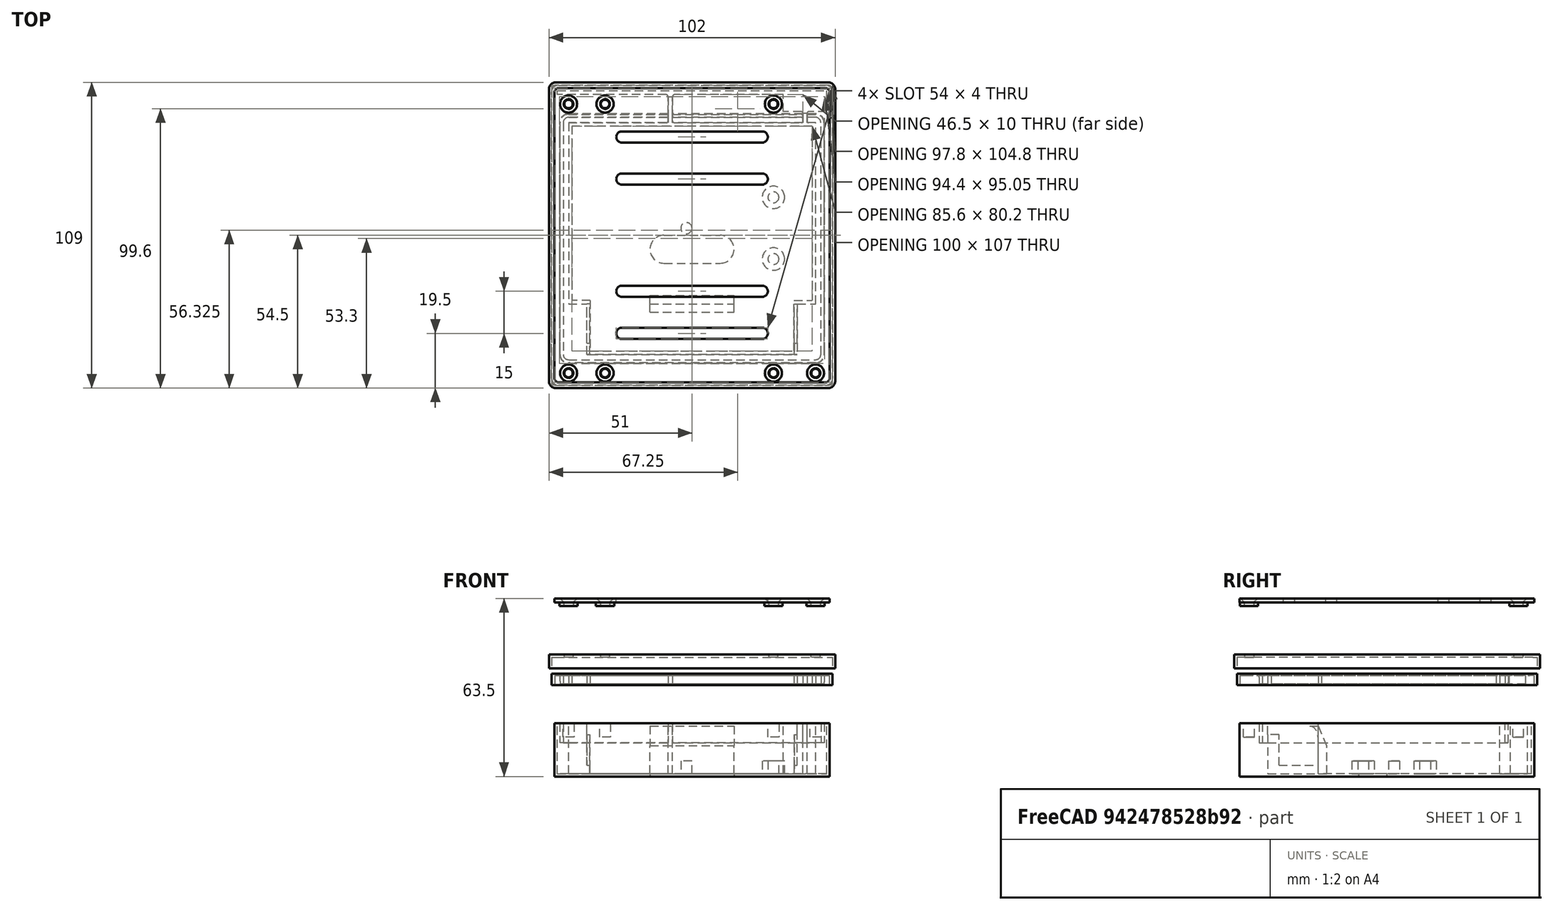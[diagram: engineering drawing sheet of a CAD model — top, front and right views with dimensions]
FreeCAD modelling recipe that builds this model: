
FCSTD DOCUMENT  (FreeCAD 1.0R39319 (Git))
Label: RAKTracker-v11
License: All rights reserved
objects: Sketcher::SketchObject×19, PartDesign::Pad×13, PartDesign::Pocket×4, PartDesign::Body×4, PartDesign::SubShapeBinder×3, PartDesign::Plane×2, Spreadsheet::Sheet×1, PartDesign::AdditiveLoft×1, PartDesign::Hole×1
note: 104 computed .brp shape members not serialized (recipe doc carries the construction recipe); baked Part::Feature solids carry a one-line shape summary decoded from their .brp

FEATURE [Spreadsheet::Sheet] Spreadsheet  label="sheet"
  cells = A1='Components; D1='None-Component sizes; D3='M3 Insert Hole Dia; E3(InsetDiaM3)==3.9 mm; A4='Solar Panel; D4='M2.5 Insert Hole DIa; E4(InsertDiaM2_5)==3.9 mm; A5='Panel width; B5(PanelWidth)==95 mm; D5='M3 Though Hall; E5(M3ThoughHoleDia)==3.2 mm; A6='Panel length; B6(PanelLength)==95 mm; D6='Insert Hole Depth; E6(InsertDepth)==8 mm; A7='Panel height; B7==1.5 mm; D8='PCB Mount Outer Diameter; E8(PCBMountDia)==8 mm; A9='Battery; D9='PCB Mount Height; E9(PCBMountHeight)==4.5 mm; A10='Battery Width; B10(BatteryWidth)==18 mm; D10='PCB Mount from Side; E10(PCBMountFromSide)==15 mm; A11='Battery Length; B11(BatteryLength)==65 mm; A12='Battery Height; B12(BatteryHeight)==18 mm; A13='Battery Mount Distance; B13(BatteryMountDistance)==75 mm; D14='Lid Wall Around sides; E14(LidWallAroundSides)==1 mm; A15='GPS Antenna Width; B15==15.5 mm; D15='Lid Wall Margin; E15==0.25 mm; A16='GPS Antenna Height; B16(AntGPSHeight)==7.5 mm; D16='Strap Mount Dia; E16(StrapMountDia)==8 mm; A17='GPS Antenna Length; B17(AntGPSLength)==15.5 mm; D17='Strap slot width; E17(StrapSlotWidth)==2 mm; D18='Strap slot distance; E18(StrapSlotDistance)==60 mm; A19='Small Molex Lora Antenna Width; B19(AntSmallLoraWidth)==10 mm; A20='Small Molex Lora Antenna Length; B20(AntSmallLoraLength)==80 mm; D20='SealWidth; E20(SealWidthTop)==1.2 mm; A21='Small Molex Lora Antenna Height; B21(AntSmallLoraHeight)==1.4 mm; D21='SealHeight; E21(SealHeight)==3 mm; D22='SealOuterWidth; E22(SealOuterWidth)==1 mm; A23='Large Molex Lora Antenna Width Sticker; B23(AntLargeLoraWidth)==12.5 mm; D23='Wall Width; E23(WallWidth)==5 mm; A24='Large Molex Lora Antenna Length Sticker; B24(AntLargeLoraLength)==87.5 mm; A25='Large Molex Lora Antenna Width (white); B25='TBD; A26='Large Molex Lora Antenna Length (white); B26==100 mm; D26='Bottom Thickness; E26(WallBottomThickness)==1 mm; A27='Large Molex Lora Antenna Height; B27(AntLargeLoraHeight)==1.6 mm; D27='Box Corner Radisu; E27(BoxCornerRadius)==1.5 mm; D28='BoxAntennaSpace; E28(BoxAntennaSpace)==10 mm; A29='Antenna Wire width; B29(AntWireWidth)==1.5 mm; A31='PCB Width; B31==30 mm; A32='PCB Length; B32==38 mm; A33='PCB Width With Margin; B33==31 mm; A34='PCB Length with Margin; B34==39 mm; A35='PCB Height; B35==16 mm; A36='PCB 2 Hole Distance; B36(PCBHoleDistance)==22 mm; A37='PCB Single Hole Distance from 2 Holes; B37(PCBHoleAwayFrom2Holes)==31 mm
FEATURE [Sketcher::SketchObject] Sketch  label="BoxBaseSketch"
  ArcFitTolerance = 1e-06
  AttachmentSupport = -> [XY_Plane]
  FullyConstrained = true
  MakeInternals = false
  MapMode = 5
  expr: Constraints[18] = <<sheet>>.BoxCornerRadius
  expr: Constraints[28] = <<sheet>>.PanelLength
  expr: Constraints[29] = <<sheet>>.PanelWidth
  expr: Constraints[31] = <<sheet>>.BoxAntennaSpace
  expr: Constraints[40] = <<sheet>>.PanelWidth / 2
  sketch-geometry (18):
    g0: LineSegment StartX=-47.5 StartY=-52.5 StartZ=0 EndX=47.5 EndY=-52.5 EndZ=0
    g1: LineSegment StartX=49 StartY=-51 StartZ=0 EndX=49 EndY=51 EndZ=0
    g2: LineSegment StartX=47.5 StartY=52.5 StartZ=0 EndX=-47.5 EndY=52.5 EndZ=0
    g3: LineSegment StartX=-49 StartY=51 StartZ=0 EndX=-49 EndY=-51 EndZ=0
    g4: ArcOfCircle CenterX=-47.5 CenterY=-51 CenterZ=0 NormalX=0 NormalY=0 NormalZ=1 AngleXU=0 Radius=1.5 StartAngle=3.14159 EndAngle=4.71239
    g5: ArcOfCircle CenterX=47.5 CenterY=-51 CenterZ=0 NormalX=0 NormalY=0 NormalZ=1 AngleXU=0 Radius=1.5 StartAngle=4.71239 EndAngle=6.28319
    g6: ArcOfCircle CenterX=47.5 CenterY=51 CenterZ=0 NormalX=0 NormalY=0 NormalZ=1 AngleXU=0 Radius=1.5 StartAngle=8e-16 EndAngle=1.5708
    g7: ArcOfCircle CenterX=-47.5 CenterY=51 CenterZ=0 NormalX=0 NormalY=0 NormalZ=1 AngleXU=0 Radius=1.5 StartAngle=1.5708 EndAngle=3.14159
    g8: GeomPoint [constr] X=49 Y=52.5 Z=0
    g9: GeomPoint [constr] X=0 Y=0 Z=0
    g10: LineSegment [constr] StartX=47.5 StartY=-52.5 StartZ=0 EndX=47.5 EndY=42.5 EndZ=0
    g11: LineSegment [constr] StartX=47.5 StartY=42.5 StartZ=0 EndX=-47.5 EndY=42.5 EndZ=0
    g12: LineSegment [constr] StartX=-47.5 StartY=42.5 StartZ=0 EndX=-47.5 EndY=-52.5 EndZ=0
    g13: LineSegment [constr] StartX=-47.5 StartY=-52.5 StartZ=0 EndX=47.5 EndY=-52.5 EndZ=0
    g14: ArcOfCircle CenterX=-10 CenterY=-5 CenterZ=0 NormalX=0 NormalY=0 NormalZ=1 AngleXU=0 Radius=5 StartAngle=1.5708 EndAngle=4.71239
    g15: ArcOfCircle CenterX=10 CenterY=-5 CenterZ=0 NormalX=0 NormalY=0 NormalZ=1 AngleXU=0 Radius=5 StartAngle=4.71239 EndAngle=7.85398
    g16: LineSegment StartX=-10 StartY=0 StartZ=0 EndX=10 EndY=0 EndZ=0
    g17: LineSegment StartX=-10 StartY=-10 StartZ=0 EndX=10 EndY=-10 EndZ=0
  constraints (41):
    c: Tangent(g0,g4) = -1.5708
    c: Tangent(g0,g5) = -1.5708
    c: Tangent(g1,g5) = -1.5708
    c: Tangent(g1,g6) = -1.5708
    c: Tangent(g2,g6) = -1.5708
    c: Tangent(g2,g7) = -1.5708
    c: Tangent(g3,g7) = -1.5708
    c: Tangent(g3,g4) = -1.5708
    c: Horizontal(g0)
    c: Horizontal(g2)
    c: Vertical(g1)
    c: Vertical(g3)
    c: Equal(g4,g5)
    c: Equal(g5,g6)
    c: Equal(g6,g7)
    c: Symmetric(g2,g0,g9)
    c: PointOnObject(g8,g1)
    c: PointOnObject(g8,g2)
    c: Radius(g5) = 1.5
    c: Coincident(g9,g-1)
    c: Coincident(g10,g11)
    c: Coincident(g11,g12)
    c: Coincident(g12,g13)
    c: Coincident(g13,g10)
    c: Vertical(g10)
    c: Vertical(g12)
    c: Horizontal(g11)
    c: Coincident(g10,g0)
    c: DistanceX(g12,g0) = 95
    c: DistanceY(g10,g10) = 95
    c: Coincident(g12,g0)
    c: DistanceY(g10,g2) = 10
    c: Tangent(g14,g16) = 1.5708
    c: Tangent(g14,g17) = -1.5708
    c: Tangent(g15,g16) = 1.5708
    c: Tangent(g15,g17) = -1.5708
    c: Equal(g14,g15)
    c: Distance(g15,g15) = 10
    c: DistanceX(g14,g15) = 20
    c: Symmetric(g14,g15,g-2)
    c: DistanceY(g15,g10) = 47.5
FEATURE [PartDesign::Pad] Pad  label="BoxBase"
  Direction = (0,0,1)
  Length = 1
  Length2 = 10
  Profile = -> Sketch
  ReferenceAxis = -> Sketch [N_Axis]
  Suppressed = false
  Type = 0
  expr: Length = <<sheet>>.WallBottomThickness
FEATURE [Sketcher::SketchObject] Sketch001  label="BoxOuterWallSketch"
  ArcFitTolerance = 1e-06
  AttachmentSupport = -> [XY_Plane]
  FullyConstrained = true
  MakeInternals = false
  MapMode = 5
  expr: Constraints[100] = <<sheet>>.PanelWidth
  expr: Constraints[101] = <<sheet>>.PanelLength
  expr: Constraints[103] = <<sheet>>.BoxAntennaSpace
  expr: Constraints[115] = <<sheet>>.BoxCornerRadius
  expr: Constraints[129] = <<sheet>>.WallWidth
  expr: Constraints[49] = <<sheet>>.AntGPSLength
  expr: Constraints[50] = <<sheet>>.AntWireWidth
  expr: Constraints[51] = <<sheet>>.BatteryMountDistance
  expr: Constraints[52] = <<sheet>>.WallWidth * 2
  expr: Constraints[53] = <<sheet>>.WallWidth
  expr: Constraints[54] = <<sheet>>.BatteryWidth
  expr: Constraints[87] = <<sheet>>.AntWireWidth
  expr: Constraints[90] = <<sheet>>.AntSmallLoraHeight
  expr: Constraints[91] = <<sheet>>.AntGPSHeight
  expr: Constraints[92] = <<sheet>>.WallWidth * 2
  sketch-geometry (48):
    g0: LineSegment StartX=-47.5 StartY=-52.5 StartZ=0 EndX=47.5 EndY=-52.5 EndZ=0
    g1: LineSegment StartX=49 StartY=-51 StartZ=0 EndX=49 EndY=51 EndZ=0
    g2: LineSegment StartX=47.5 StartY=52.5 StartZ=0 EndX=-47.5 EndY=52.5 EndZ=0
    g3: LineSegment StartX=44 StartY=40.1 StartZ=0 EndX=44 EndY=-24.5 EndZ=0
    g4: LineSegment StartX=44 StartY=-24.5 StartZ=0 EndX=37.5 EndY=-24.5 EndZ=0
    g5: LineSegment StartX=37.5 StartY=-24.5 StartZ=0 EndX=37.5 EndY=-42.5 EndZ=0
    g6: LineSegment StartX=37.5 StartY=-42.5 StartZ=0 EndX=-37.5 EndY=-42.5 EndZ=0
    g7: LineSegment StartX=-37.5 StartY=-42.5 StartZ=0 EndX=-37.5 EndY=-24.5 EndZ=0
    g8: LineSegment StartX=-37.5 StartY=-24.5 StartZ=0 EndX=-44 EndY=-24.5 EndZ=0
    g9: LineSegment StartX=-44 StartY=-24.5 StartZ=0 EndX=-44 EndY=40.1 EndZ=0
    g10: LineSegment StartX=-44 StartY=40.1 StartZ=0 EndX=-9.25 EndY=40.1 EndZ=0
    g11: LineSegment StartX=-8.5 StartY=40.85 StartZ=0 EndX=-8.5 EndY=49.35 EndZ=0
    g12: LineSegment StartX=-9.25 StartY=50.1 StartZ=0 EndX=-48 EndY=50.1 EndZ=0
    g13: LineSegment StartX=-48 StartY=50.1 StartZ=0 EndX=-48 EndY=51.5 EndZ=0
    g14: LineSegment StartX=-48 StartY=51.5 StartZ=0 EndX=48 EndY=51.5 EndZ=0
    g15: LineSegment StartX=-7 StartY=40.85 StartZ=0 EndX=-7 EndY=49.35 EndZ=0
    g16: LineSegment StartX=-6.25 StartY=50.1 StartZ=0 EndX=32.5 EndY=50.1 EndZ=0
    g17: LineSegment StartX=32.5 StartY=50.1 StartZ=0 EndX=32.5 EndY=44 EndZ=0
    g18: LineSegment StartX=48 StartY=44 StartZ=0 EndX=48 EndY=51.5 EndZ=0
    g19: ArcOfCircle CenterX=-9.25 CenterY=49.35 CenterZ=0 NormalX=0 NormalY=0 NormalZ=1 AngleXU=0 Radius=0.75 StartAngle=2e-15 EndAngle=1.5708
    g20: GeomPoint [constr] X=-8.5 Y=50.1 Z=0
    g21: ArcOfCircle CenterX=-6.25 CenterY=49.35 CenterZ=0 NormalX=0 NormalY=0 NormalZ=1 AngleXU=0 Radius=0.75 StartAngle=1.5708 EndAngle=3.14159
    g22: ArcOfCircle CenterX=-9.25 CenterY=40.85 CenterZ=0 NormalX=0 NormalY=0 NormalZ=1 AngleXU=0 Radius=0.75 StartAngle=4.71239 EndAngle=6.28319
    g23: GeomPoint [constr] X=-8.5 Y=40.1 Z=0
    g24: ArcOfCircle CenterX=-6.25 CenterY=40.85 CenterZ=0 NormalX=0 NormalY=0 NormalZ=1 AngleXU=0 Radius=0.75 StartAngle=3.14159 EndAngle=4.71239
    g25: LineSegment StartX=32.5 StartY=44 StartZ=0 EndX=39 EndY=44 EndZ=0
    g26: LineSegment StartX=39.5 StartY=43.5 StartZ=0 EndX=39.5 EndY=40.6 EndZ=0
    g27: LineSegment StartX=39 StartY=40.1 StartZ=0 EndX=-6.25 EndY=40.1 EndZ=0
    g28: LineSegment StartX=48 StartY=44 StartZ=0 EndX=41.5 EndY=44 EndZ=0
    g29: LineSegment StartX=41 StartY=43.5 StartZ=0 EndX=41 EndY=40.6 EndZ=0
    g30: LineSegment StartX=41.5 StartY=40.1 StartZ=0 EndX=44 EndY=40.1 EndZ=0
    g31: ArcOfCircle CenterX=39 CenterY=43.5 CenterZ=0 NormalX=0 NormalY=0 NormalZ=1 AngleXU=0 Radius=0.5 StartAngle=-1.8e-15 EndAngle=1.5708
    g32: GeomPoint [constr] X=39.5 Y=44 Z=0
    g33: ArcOfCircle CenterX=41.5 CenterY=43.5 CenterZ=0 NormalX=0 NormalY=0 NormalZ=1 AngleXU=0 Radius=0.5 StartAngle=1.5708 EndAngle=3.14159
    g34: GeomPoint [constr] X=41 Y=44 Z=0
    g35: ArcOfCircle CenterX=39 CenterY=40.6 CenterZ=0 NormalX=0 NormalY=0 NormalZ=1 AngleXU=0 Radius=0.5 StartAngle=4.71239 EndAngle=6.28319
    g36: GeomPoint [constr] X=39.5 Y=40.1 Z=0
    g37: ArcOfCircle CenterX=41.5 CenterY=40.6 CenterZ=0 NormalX=0 NormalY=0 NormalZ=1 AngleXU=0 Radius=0.5 StartAngle=3.14159 EndAngle=4.71239
    g38: GeomPoint [constr] X=41 Y=40.1 Z=0
    g39: LineSegment [constr] StartX=-47.5 StartY=42.5 StartZ=0 EndX=-47.5 EndY=-52.5 EndZ=0
    g40: LineSegment [constr] StartX=-47.5 StartY=-52.5 StartZ=0 EndX=47.5 EndY=-52.5 EndZ=0
    g41: LineSegment [constr] StartX=47.5 StartY=-52.5 StartZ=0 EndX=47.5 EndY=42.5 EndZ=0
    g42: LineSegment [constr] StartX=47.5 StartY=42.5 StartZ=0 EndX=-47.5 EndY=42.5 EndZ=0
    g43: LineSegment StartX=-49 StartY=51 StartZ=0 EndX=-49 EndY=-51 EndZ=0
    g44: ArcOfCircle CenterX=-47.5 CenterY=-51 CenterZ=0 NormalX=0 NormalY=0 NormalZ=1 AngleXU=0 Radius=1.5 StartAngle=3.14159 EndAngle=4.71239
    g45: ArcOfCircle CenterX=47.5 CenterY=-51 CenterZ=0 NormalX=0 NormalY=0 NormalZ=1 AngleXU=0 Radius=1.5 StartAngle=4.71239 EndAngle=6.28319
    g46: ArcOfCircle CenterX=47.5 CenterY=51 CenterZ=0 NormalX=0 NormalY=0 NormalZ=1 AngleXU=0 Radius=1.5 StartAngle=0 EndAngle=1.5708
    g47: ArcOfCircle CenterX=-47.5 CenterY=51 CenterZ=0 NormalX=0 NormalY=0 NormalZ=1 AngleXU=0 Radius=1.5 StartAngle=1.5708 EndAngle=3.14159
  constraints (132):
    c: Vertical(g1)
    c: Horizontal(g2)
    c: Vertical(g3)
    c: Coincident(g3,g4)
    c: Horizontal(g4)
    c: Coincident(g4,g5)
    c: Vertical(g5)
    c: Coincident(g5,g6)
    c: Horizontal(g6)
    c: Coincident(g6,g7)
    c: Vertical(g7)
    c: Coincident(g7,g8)
    c: Coincident(g8,g9)
    c: Vertical(g9)
    c: Coincident(g9,g10)
    c: Horizontal(g10)
    c: Coincident(g12,g13)
    c: Coincident(g13,g14)
    c: Horizontal(g14)
    c: Horizontal(g8)
    c: Vertical(g15)
    c: Horizontal(g16)
    c: Coincident(g16,g17)
    c: Coincident(g18,g14)
    c: Vertical(g18)
    c: Vertical(g17)
    c: Vertical(g11)
    c: Vertical(g13)
    c: Horizontal(g12)
    c: PointOnObject(g20,g12)
    c: PointOnObject(g20,g11)
    c: Tangent(g12,g19) = -1.5708
    c: Tangent(g11,g19) = -1.5708
    c: Tangent(g15,g21) = 1.5708
    c: Tangent(g16,g21) = 1.5708
    c: PointOnObject(g23,g11)
    c: PointOnObject(g23,g10)
    c: Tangent(g11,g22) = -1.5708
    c: Tangent(g10,g22) = -1.5708
    c: Tangent(g15,g24) = 1.5708
    c: Radius(g19) = 0.75
    c: Equal(g19,g22)
    c: Equal(g22,g21)
    c: Equal(g21,g24)
    c: Horizontal(g11,g15)
    c: Horizontal(g7,g4)
    c: Equal(g8,g4)
    c: DistanceY(g13,g2) = 1
    c: DistanceX(g14,g1) = 1
    c: DistanceX(g17,g18) = 15.5
    c: DistanceX(g11,g15) = 1.5
    c: DistanceX(g7,g4) = 75
    c: DistanceY(g0,g6) = 10
    c: DistanceX(g3,g1) = 5
    c: DistanceY(g5,g4) = 18
    c: Coincident(g17,g25)
    c: Coincident(g27,g24)
    c: Horizontal(g27)
    c: Coincident(g18,g28)
    c: Horizontal(g28)
    c: Coincident(g30,g3)
    c: Horizontal(g25)
    c: Vertical(g29)
    c: Vertical(g26)
    c: Horizontal(g30)
    c: PointOnObject(g32,g25)
    c: PointOnObject(g32,g26)
    c: Tangent(g25,g31) = 1.5708
    c: Tangent(g26,g31) = 1.5708
    c: PointOnObject(g34,g29)
    c: PointOnObject(g34,g28)
    c: Tangent(g29,g33) = -1.5708
    c: Tangent(g28,g33) = -1.5708
    c: PointOnObject(g36,g26)
    c: PointOnObject(g36,g27)
    c: Tangent(g26,g35) = 1.5708
    c: Tangent(g27,g35) = 1.5708
    c: PointOnObject(g38,g30)
    c: PointOnObject(g38,g29)
    c: Tangent(g30,g37) = -1.5708
    c: Tangent(g29,g37) = -1.5708
    c: Radius(g31) = 0.5
    c: Equal(g31,g33)
    c: Equal(g33,g35)
    c: Equal(g35,g37)
    c: Horizontal(g30,g27)
    c: Horizontal(g25,g28)
    c: DistanceX(g26,g29) = 1.5
    c: Equal(g25,g28)
    c: Horizontal(g10,g24)
    c: DistanceY(g12,g13) = 1.4
    c: DistanceY(g18,g14) = 7.5
    c: DistanceY(g9,g12) = 10
    c: Coincident(g39,g40)
    c: Coincident(g41,g42)
    c: Coincident(g42,g39)
    c: Vertical(g39)
    c: Vertical(g41)
    c: Horizontal(g42)
    c: Horizontal(g0)
    c: DistanceY(g39,g39) = 95
    c: DistanceX(g40,g40) = 95
    c: Coincident(g41,g40)
    c: DistanceY(g41,g2) = 10
    c: Coincident(g0,g39)
    c: Coincident(g0,g40)
    c: Vertical(g43)
    c: Coincident(g44,g0)
    c: Coincident(g44,g43)
    c: Coincident(g45,g0)
    c: Coincident(g45,g1)
    c: Coincident(g46,g2)
    c: Coincident(g46,g1)
    c: Coincident(g47,g43)
    c: Coincident(g47,g2)
    c: Radius(g47) = 1.5
    c: Horizontal(g47,g43)
    c: Vertical(g47,g2)
    c: Equal(g47,g46)
    c: Vertical(g2,g46)
    c: Horizontal(g1,g46)
    c: Vertical(g44,g0)
    c: Horizontal(g43,g44)
    c: Horizontal(g1,g45)
    c: Vertical(g0,g45)
    c: DistanceX(g43,g12) = 1
    c: Symmetric(g2,g0,g-1)
    c: Vertical(g39,g47)
    c: Vertical(g41,g46)
    c: DistanceX(g43,g8) = 5
    c: DistanceX(g12,g11) = 39.5
    c: Horizontal(g12,g16)
FEATURE [PartDesign::Pad] Pad001  label="BoxWall"
  BaseFeature = -> Pad
  Direction = (0,0,1)
  Length = 19
  Length2 = 10
  Profile = -> Sketch001
  ReferenceAxis = -> Sketch001 [N_Axis]
  Suppressed = false
  Type = 0
  expr: Length = <<sheet>>.BatteryWidth + <<sheet>>.WallBottomThickness
FEATURE [Sketcher::SketchObject] Sketch002  label="BoxPCBMountSketch"
  ArcFitTolerance = 1e-06
  AttachmentSupport = -> [XY_Plane]
  ExternalGeometry = -> [Sketch001]
  FullyConstrained = true
  MakeInternals = false
  MapMode = 5
  expr: Constraints[10] = <<sheet>>.PCBHoleDistance / 2
  expr: Constraints[11] = <<sheet>>.PCBMountFromSide
  expr: Constraints[2] = <<sheet>>.InsetDiaM3
  expr: Constraints[5] = <<sheet>>.PCBMountDia
  expr: Constraints[7] = <<sheet>>.PCBHoleDistance
  expr: Constraints[8] = <<sheet>>.PCBHoleAwayFrom2Holes
  expr: Constraints[9] = <<sheet>>.PCBMountDia / 2
  sketch-geometry (5):
    g0: Circle CenterX=29 CenterY=13.5 CenterZ=0 NormalX=0 NormalY=0 NormalZ=1 AngleXU=0 Radius=4
    g1: Circle CenterX=29 CenterY=-8.5 CenterZ=0 NormalX=0 NormalY=0 NormalZ=1 AngleXU=0 Radius=4
    g2: Circle CenterX=29 CenterY=-8.5 CenterZ=0 NormalX=0 NormalY=0 NormalZ=1 AngleXU=0 Radius=1.95
    g3: Circle CenterX=29 CenterY=13.5 CenterZ=0 NormalX=0 NormalY=0 NormalZ=1 AngleXU=0 Radius=1.95
    g4: Circle CenterX=-2 CenterY=2.5 CenterZ=0 NormalX=0 NormalY=0 NormalZ=1 AngleXU=0 Radius=2
  constraints (13):
    c: Coincident(g2,g1)
    c: Coincident(g3,g0)
    c: Diameter(g3) = 3.9
    c: Equal(g3,g2)
    c: Vertical(g1,g0)
    c: Diameter(g0) = 8
    c: Equal(g0,g1)
    c: DistanceY(g1,g0) = 22
    c: DistanceX(g4,g1) = 31
    c: Diameter(g4) = 4
    c: DistanceY(g1,g4) = 11
    c: DistanceX(g1,g-3) = 15
    c: DistanceY(g-3,g1) = 16
FEATURE [PartDesign::Pad] Pad002  label="BoxPCBMount"
  BaseFeature = -> Pad001
  Direction = (0,0,1)
  Length = 5.5
  Length2 = 10
  Profile = -> Sketch002
  ReferenceAxis = -> Sketch002 [N_Axis]
  Suppressed = false
  Type = 0
  expr: Length = <<sheet>>.WallBottomThickness + <<sheet>>.PCBMountHeight
FEATURE [Sketcher::SketchObject] Sketch003  label="BoxBatteryHolderSketch"
  ArcFitTolerance = 1e-06
  AttachmentSupport = -> [YZ_Plane]
  ExternalGeometry = -> [Sketch001]
  FullyConstrained = true
  MakeInternals = false
  MapMode = 5
  Placement = pos=(0,0,0) rot=(0.57735,0.57735,0.57735;2.0944rad)
  expr: Constraints[21] = <<sheet>>.BatteryWidth
  sketch-geometry (11):
    g0: LineSegment StartX=-24.5 StartY=0 StartZ=0 EndX=-24.5 EndY=11 EndZ=0
    g1: LineSegment StartX=-24.5 StartY=0 StartZ=0 EndX=-21.5 EndY=0 EndZ=0
    g2: LineSegment StartX=-21.5 StartY=0 StartZ=0 EndX=-21.5 EndY=11 EndZ=0
    g3: Circle [constr] CenterX=-27.5 CenterY=18 CenterZ=0 NormalX=0 NormalY=0 NormalZ=1 AngleXU=0 Radius=1
    g4: Circle [constr] CenterX=-24.5 CenterY=18 CenterZ=0 NormalX=0 NormalY=0 NormalZ=1 AngleXU=0 Radius=1
    g5: Circle [constr] CenterX=-24.5 CenterY=11 CenterZ=0 NormalX=0 NormalY=0 NormalZ=1 AngleXU=0 Radius=1
    g6: BSplineCurve PolesCount=3 KnotsCount=2 Degree=2 IsPeriodic=0
    g7: GeomPoint [constr] X=-27.5 Y=18 Z=0
    g8: GeomPoint [constr] X=-24.5 Y=11 Z=0
    g9: LineSegment StartX=-27.5 StartY=18 StartZ=0 EndX=-24.5 EndY=18 EndZ=0
    g10: LineSegment StartX=-24.5 StartY=18 StartZ=0 EndX=-21.5 EndY=11 EndZ=0
  constraints (26):
    c: Coincident(g0,g-3)
    c: Vertical(g0)
    c: Coincident(g1,g0)
    c: PointOnObject(g1,g-1)
    c: Coincident(g2,g1)
    c: Vertical(g2)
    c: Weight(g3) = 1
    c: Equal(g3,g4)
    c: Equal(g3,g5)
    c: InternalAlignment(g3,g6)
    c: InternalAlignment(g4,g6)
    c: InternalAlignment(g5,g6)
    c: InternalAlignment(g7,g6)
    c: InternalAlignment(g8,g6)
    c: Coincident(g6,g0)
    c: DistanceX(g1,g1) = 3
    c: DistanceY(g0,g0) = 11
    c: Coincident(g9,g6)
    c: Horizontal(g9)
    c: Coincident(g10,g9)
    c: Coincident(g10,g2)
    c: DistanceY(g1,g9) = 18
    c: Horizontal(g0,g2)
    c: DistanceX(g6,g9) = 3
    c: Vertical(g0,g9)
    c: Coincident(g4,g9)
FEATURE [PartDesign::Pad] Pad003  label="BoxBatteryHolder"
  BaseFeature = -> Pad002
  Direction = (1,0,0)
  Length = 30
  Length2 = 10
  Midplane = true
  Profile = -> Sketch003
  ReferenceAxis = -> Sketch003 [N_Axis]
  Suppressed = false
  Type = 0
FEATURE [Sketcher::SketchObject] Sketch004  label="BoxSealPocketSketch"
  ArcFitTolerance = 1e-06
  AttachmentSupport = -> [Pad003]
  ExternalGeometry = -> [Sketch001]
  FullyConstrained = true
  MakeInternals = false
  MapMode = 5
  Placement = pos=(0,0,19) rot=(0,0,1;0rad)
  expr: Constraints[33] = <<sheet>>.SealWidthTop
  expr: Constraints[34] = (<<sheet>>.WallWidth - <<sheet>>.SealWidthTop) / 2
  expr: Constraints[35] = (<<sheet>>.WallWidth - <<sheet>>.SealWidthTop) / 2
  expr: Constraints[38] = (<<sheet>>.WallWidth - <<sheet>>.SealWidthTop) / 2
  sketch-geometry (18):
    g0: LineSegment StartX=47.1 StartY=-42.5 StartZ=0 EndX=47.1 EndY=40.1 EndZ=0
    g1: LineSegment StartX=44 StartY=43.2 StartZ=0 EndX=-44 EndY=43.2 EndZ=0
    g2: LineSegment StartX=-47.1 StartY=40.1 StartZ=0 EndX=-47.1 EndY=-42.5 EndZ=0
    g3: LineSegment StartX=-44 StartY=-45.6 StartZ=0 EndX=44 EndY=-45.6 EndZ=0
    g4: ArcOfCircle CenterX=44 CenterY=-42.5 CenterZ=0 NormalX=0 NormalY=0 NormalZ=1 AngleXU=0 Radius=3.1 StartAngle=4.71239 EndAngle=6.28319
    g5: ArcOfCircle CenterX=44 CenterY=40.1 CenterZ=0 NormalX=0 NormalY=0 NormalZ=1 AngleXU=0 Radius=3.1 StartAngle=8e-16 EndAngle=1.5708
    g6: ArcOfCircle CenterX=-44 CenterY=40.1 CenterZ=0 NormalX=0 NormalY=0 NormalZ=1 AngleXU=0 Radius=3.1 StartAngle=1.5708 EndAngle=3.14159
    g7: ArcOfCircle CenterX=-44 CenterY=-42.5 CenterZ=0 NormalX=0 NormalY=0 NormalZ=1 AngleXU=0 Radius=3.1 StartAngle=3.14159 EndAngle=4.71239
    g8: LineSegment StartX=45.9 StartY=-42.5 StartZ=0 EndX=45.9 EndY=40.1 EndZ=0
    g9: LineSegment StartX=44 StartY=42 StartZ=0 EndX=-44 EndY=42 EndZ=0
    g10: LineSegment StartX=-45.9 StartY=40.1 StartZ=0 EndX=-45.9 EndY=-42.5 EndZ=0
    g11: LineSegment StartX=-44 StartY=-44.4 StartZ=0 EndX=44 EndY=-44.4 EndZ=0
    g12: ArcOfCircle CenterX=44 CenterY=-42.5 CenterZ=0 NormalX=0 NormalY=0 NormalZ=1 AngleXU=0 Radius=1.9 StartAngle=4.71239 EndAngle=6.28319
    g13: ArcOfCircle CenterX=44 CenterY=40.1 CenterZ=0 NormalX=0 NormalY=0 NormalZ=1 AngleXU=0 Radius=1.9 StartAngle=-9e-16 EndAngle=1.5708
    g14: ArcOfCircle CenterX=-44 CenterY=40.1 CenterZ=0 NormalX=0 NormalY=0 NormalZ=1 AngleXU=0 Radius=1.9 StartAngle=1.5708 EndAngle=3.14159
    g15: ArcOfCircle CenterX=-44 CenterY=-42.5 CenterZ=0 NormalX=0 NormalY=0 NormalZ=1 AngleXU=0 Radius=1.9 StartAngle=3.14159 EndAngle=4.71239
    g16: GeomPoint [constr] X=-47.1 Y=43.2 Z=0
    g17: GeomPoint [constr] X=0 Y=0 Z=0
  constraints (39):
    c: Tangent(g0,g4) = -1.5708
    c: Tangent(g0,g5) = -1.5708
    c: Tangent(g1,g5) = -1.5708
    c: Tangent(g1,g6) = -1.5708
    c: Tangent(g2,g6) = -1.5708
    c: Tangent(g2,g7) = -1.5708
    c: Tangent(g3,g7) = -1.5708
    c: Tangent(g3,g4) = -1.5708
    c: Vertical(g0)
    c: Vertical(g2)
    c: Horizontal(g1)
    c: Horizontal(g3)
    c: Equal(g4,g5)
    c: Equal(g5,g6)
    c: Equal(g6,g7)
    c: Tangent(g8,g12) = -1.5708
    c: Tangent(g8,g13) = -1.5708
    c: Tangent(g9,g13) = -1.5708
    c: Tangent(g9,g14) = -1.5708
    c: Tangent(g10,g14) = -1.5708
    c: Tangent(g10,g15) = -1.5708
    c: Tangent(g11,g15) = -1.5708
    c: Tangent(g11,g12) = -1.5708
    c: Coincident(g4,g12)
    c: Coincident(g5,g13)
    c: Coincident(g6,g14)
    c: Coincident(g7,g15)
    c: Vertical(g8)
    c: Vertical(g10)
    c: Horizontal(g9)
    c: PointOnObject(g16,g1)
    c: PointOnObject(g16,g2)
    c: Coincident(g17,g-1)
    c: DistanceY(g9,g1) = 1.2
    c: DistanceY(g11,g-4) = 1.9
    c: DistanceY(g-3,g9) = 1.9
    c: Vertical(g-3,g9)
    c: Horizontal(g10,g-3)
    c: DistanceX(g-5,g8) = 1.9
FEATURE [PartDesign::Pocket] Pocket  label="BoxSealPocket"
  BaseFeature = -> Pad003
  Direction = (0,0,-1)
  Length = 7
  Length2 = 5
  Profile = -> Sketch004
  ReferenceAxis = -> Sketch004 [N_Axis]
  Suppressed = false
  Type = 0
FEATURE [Sketcher::SketchObject] Sketch005  label="BoxBatteryClip1Sketch"
  ArcFitTolerance = 1e-06
  AttachmentOffset = pos=(0,0,36.5) rot=(0,0,1;0rad)
  AttachmentSupport = -> [YZ_Plane]
  ExternalGeometry = -> [Sketch001]
  FullyConstrained = true
  MakeInternals = false
  MapMode = 5
  Placement = pos=(36.5,0,0) rot=(0.57735,0.57735,0.57735;2.0944rad)
  expr: .AttachmentOffset.Base.z = <<sheet>>.BatteryMountDistance / 2 - 1 mm
  expr: Constraints[15] = <<sheet>>.BatteryWidth - <<sheet>>.SealHeight
  sketch-geometry (6):
    g0: LineSegment StartX=-24.5 StartY=0 StartZ=0 EndX=-24.5 EndY=4 EndZ=0
    g1: LineSegment StartX=-38.5 StartY=4 StartZ=0 EndX=-24.5 EndY=4 EndZ=0
    g2: LineSegment StartX=-38.5 StartY=4 StartZ=0 EndX=-38.5 EndY=15 EndZ=0
    g3: LineSegment StartX=-38.5 StartY=15 StartZ=0 EndX=-42.5 EndY=15 EndZ=0
    g4: LineSegment StartX=-42.5 StartY=15 StartZ=0 EndX=-42.5 EndY=0 EndZ=0
    g5: LineSegment StartX=-42.5 StartY=0 StartZ=0 EndX=-24.5 EndY=0 EndZ=0
  constraints (16):
    c: Coincident(g-3,g0)
    c: Vertical(g0)
    c: Coincident(g1,g0)
    c: Horizontal(g1)
    c: Coincident(g1,g2)
    c: Vertical(g2)
    c: Coincident(g2,g3)
    c: Horizontal(g3)
    c: Coincident(g3,g4)
    c: Coincident(g4,g-3)
    c: Coincident(g4,g5)
    c: Coincident(g5,g0)
    c: Vertical(g4)
    c: DistanceX(g3,g3) = 4
    c: DistanceY(g0,g0) = 4
    c: DistanceY(g4,g3) = 15
FEATURE [PartDesign::Pad] Pad004  label="BoxBatteryClip1"
  BaseFeature = -> Pocket
  Direction = (1,0,0)
  Length = 1
  Length2 = 10
  Profile = -> Sketch005
  ReferenceAxis = -> Sketch005 [N_Axis]
  Suppressed = false
  Type = 0
FEATURE [Sketcher::SketchObject] Sketch006  label="BoxBatteryClip2Sketch"
  ArcFitTolerance = 1e-06
  AttachmentOffset = pos=(0,0,-37.5) rot=(0,0,1;0rad)
  AttachmentSupport = -> [YZ_Plane]
  ExternalGeometry = -> [Sketch001]
  FullyConstrained = true
  MakeInternals = false
  MapMode = 5
  Placement = pos=(-37.5,0,0) rot=(0.57735,0.57735,0.57735;2.0944rad)
  expr: .AttachmentOffset.Base.z = <<sheet>>.BatteryMountDistance / 2 mm * -1 mm
  expr: Constraints[14] = <<sheet>>.BatteryWidth - <<sheet>>.SealHeight
  sketch-geometry (6):
    g0: LineSegment StartX=-42.5 StartY=0 StartZ=0 EndX=-42.5 EndY=15 EndZ=0
    g1: LineSegment StartX=-42.5 StartY=15 StartZ=0 EndX=-38.5 EndY=15 EndZ=0
    g2: LineSegment StartX=-38.5 StartY=15 StartZ=0 EndX=-38.5 EndY=4 EndZ=0
    g3: LineSegment StartX=-38.5 StartY=4 StartZ=0 EndX=-24.5 EndY=4 EndZ=0
    g4: LineSegment StartX=-24.5 StartY=4 StartZ=0 EndX=-24.5 EndY=0 EndZ=0
    g5: LineSegment StartX=-24.5 StartY=0 StartZ=0 EndX=-42.5 EndY=0 EndZ=0
  constraints (16):
    c: Coincident(g-3,g0)
    c: Vertical(g0)
    c: Coincident(g0,g1)
    c: Coincident(g1,g2)
    c: Coincident(g2,g3)
    c: Coincident(g3,g4)
    c: Coincident(g4,g-3)
    c: Coincident(g4,g5)
    c: Coincident(g5,g0)
    c: Horizontal(g3)
    c: Vertical(g4)
    c: Vertical(g2)
    c: Horizontal(g1)
    c: DistanceY(g4,g4) = 4
    c: DistanceY(g0,g0) = 15
    c: DistanceX(g0,g1) = 4
FEATURE [PartDesign::Plane] DatumPlane  label="BoxTop"
  Length = 118.288
  MapMode = 5
  Placement = pos=(0,0,19) rot=(0,0,1;0rad)
  ResizeMode = 0
  Width = 125.288
FEATURE [Sketcher::SketchObject] Sketch007  label="BoxLidHolesSketch"
  ArcFitTolerance = 1e-06
  AttachmentSupport = -> [DatumPlane]
  ExternalGeometry = -> [Sketch001]
  FullyConstrained = true
  MakeInternals = false
  MapMode = 5
  Placement = pos=(0,0,19) rot=(0,0,1;0rad)
  expr: Constraints[15] = <<sheet>>.WallWidth / 3 * 2
  expr: Constraints[16] = <<sheet>>.WallWidth / 3 * 2
  expr: Constraints[17] = <<sheet>>.WallWidth
  expr: Constraints[18] = <<sheet>>.WallWidth
  expr: Constraints[8] = <<sheet>>.InsetDiaM3
  sketch-geometry (7):
    g0: Circle CenterX=-44 CenterY=-49.1667 CenterZ=0 NormalX=0 NormalY=0 NormalZ=1 AngleXU=0 Radius=1.95
    g1: Circle CenterX=44 CenterY=-49.1667 CenterZ=0 NormalX=0 NormalY=0 NormalZ=1 AngleXU=0 Radius=1.95
    g2: Circle CenterX=-44 CenterY=46.7667 CenterZ=0 NormalX=0 NormalY=0 NormalZ=1 AngleXU=0 Radius=1.95
    g3: Circle CenterX=29 CenterY=46.7667 CenterZ=0 NormalX=0 NormalY=0 NormalZ=1 AngleXU=0 Radius=1.95
    g4: Circle CenterX=-31 CenterY=46.7667 CenterZ=0 NormalX=0 NormalY=0 NormalZ=1 AngleXU=0 Radius=1.95
    g5: Circle CenterX=29 CenterY=-49.1667 CenterZ=0 NormalX=0 NormalY=0 NormalZ=1 AngleXU=0 Radius=1.95
    g6: Circle CenterX=-31 CenterY=-49.1667 CenterZ=0 NormalX=0 NormalY=0 NormalZ=1 AngleXU=0 Radius=1.95
  constraints (21):
    c: Horizontal(g6,g5)
    c: Horizontal(g5,g1)
    c: Horizontal(g1,g0)
    c: DistanceX(g6,g5) = 60
    c: Vertical(g6,g4)
    c: Vertical(g3,g5)
    c: Vertical(g0,g2)
    c: Horizontal(g2,g4)
    c: Diameter(g0) = 3.9
    c: Equal(g0,g1)
    c: Equal(g1,g2)
    c: Equal(g2,g3)
    c: Equal(g3,g4)
    c: Equal(g4,g5)
    c: Equal(g5,g6)
    c: DistanceY(g-3,g0) = 3.33333
    c: DistanceY(g2,g-4) = 3.33333
    c: DistanceX(g1,g-6) = 5
    c: DistanceX(g-5,g0) = 5
    c: Horizontal(g4,g3)
    c: Distance(g4,g-2) = 31
FEATURE [PartDesign::Pocket] Pocket001  label="BoxLidHoles"
  BaseFeature = -> Pad004
  Direction = (0,0,-1)
  Length = 5
  Length2 = 5
  Profile = -> Sketch007
  ReferenceAxis = -> Sketch007 [N_Axis]
  Suppressed = false
  Type = 0
FEATURE [Sketcher::SketchObject] Sketch008  label="SealBaseSketch"
  ArcFitTolerance = 1e-06
  AttachmentSupport = -> [XY_Plane001]
  FullyConstrained = true
  MakeInternals = false
  MapMode = 5
  expr: Constraints[19] = <<sheet>>.BoxCornerRadius
  expr: Constraints[29] = <<sheet>>.PanelWidth
  expr: Constraints[30] = <<sheet>>.PanelLength
  expr: Constraints[31] = <<sheet>>.BoxAntennaSpace
  sketch-geometry (14):
    g0: LineSegment StartX=-49 StartY=51 StartZ=0 EndX=-49 EndY=-51 EndZ=0
    g1: LineSegment StartX=-47.5 StartY=-52.5 StartZ=0 EndX=47.5 EndY=-52.5 EndZ=0
    g2: LineSegment StartX=49 StartY=-51 StartZ=0 EndX=49 EndY=51 EndZ=0
    g3: LineSegment StartX=47.5 StartY=52.5 StartZ=0 EndX=-47.5 EndY=52.5 EndZ=0
    g4: ArcOfCircle CenterX=-47.5 CenterY=51 CenterZ=0 NormalX=0 NormalY=0 NormalZ=1 AngleXU=0 Radius=1.5 StartAngle=1.5708 EndAngle=3.14159
    g5: ArcOfCircle CenterX=-47.5 CenterY=-51 CenterZ=0 NormalX=0 NormalY=0 NormalZ=1 AngleXU=0 Radius=1.5 StartAngle=3.14159 EndAngle=4.71239
    g6: ArcOfCircle CenterX=47.5 CenterY=-51 CenterZ=0 NormalX=0 NormalY=0 NormalZ=1 AngleXU=0 Radius=1.5 StartAngle=4.71239 EndAngle=6.28319
    g7: ArcOfCircle CenterX=47.5 CenterY=51 CenterZ=0 NormalX=0 NormalY=0 NormalZ=1 AngleXU=0 Radius=1.5 StartAngle=-9e-16 EndAngle=1.5708
    g8: GeomPoint [constr] X=-49 Y=52.5 Z=0
    g9: GeomPoint [constr] X=49 Y=-52.5 Z=0
    g10: LineSegment [constr] StartX=-47.5 StartY=-52.5 StartZ=0 EndX=47.5 EndY=-52.5 EndZ=0
    g11: LineSegment [constr] StartX=47.5 StartY=-52.5 StartZ=0 EndX=47.5 EndY=42.5 EndZ=0
    g12: LineSegment [constr] StartX=47.5 StartY=42.5 StartZ=0 EndX=-47.5 EndY=42.5 EndZ=0
    g13: LineSegment [constr] StartX=-47.5 StartY=42.5 StartZ=0 EndX=-47.5 EndY=-52.5 EndZ=0
  constraints (33):
    c: Tangent(g0,g4) = -1.5708
    c: Tangent(g0,g5) = -1.5708
    c: Tangent(g1,g5) = -1.5708
    c: Tangent(g1,g6) = -1.5708
    c: Tangent(g2,g6) = -1.5708
    c: Tangent(g2,g7) = -1.5708
    c: Tangent(g3,g7) = -1.5708
    c: Tangent(g3,g4) = -1.5708
    c: Vertical(g0)
    c: Vertical(g2)
    c: Horizontal(g1)
    c: Horizontal(g3)
    c: Equal(g4,g5)
    c: Equal(g5,g6)
    c: Equal(g6,g7)
    c: PointOnObject(g8,g0)
    c: PointOnObject(g8,g3)
    c: PointOnObject(g9,g1)
    c: PointOnObject(g9,g2)
    c: Radius(g5) = 1.5
    c: Coincident(g10,g11)
    c: Coincident(g11,g12)
    c: Coincident(g12,g13)
    c: Coincident(g13,g10)
    c: Horizontal(g12)
    c: Vertical(g11)
    c: Vertical(g13)
    c: Coincident(g10,g1)
    c: Coincident(g10,g1)
    c: DistanceY(g11,g11) = 95
    c: DistanceX(g12,g12) = 95
    c: DistanceY(g11,g3) = 10
    c: Symmetric(g3,g1,g-1)
FEATURE [PartDesign::Pad] Pad006  label="SealBase"
  Direction = (0,0,1)
  Length = 0.6
  Length2 = 10
  Profile = -> Sketch008
  ReferenceAxis = -> Sketch008 [N_Axis]
  Suppressed = false
  Type = 0
FEATURE [Sketcher::SketchObject] Sketch009  label="SealTopSketch"
  ArcFitTolerance = 1e-06
  AttachmentSupport = -> [XY_Plane001]
  ExternalGeometry = -> [Sketch008]
  FullyConstrained = true
  MakeInternals = false
  MapMode = 5
  expr: Constraints[10] = <<sheet>>.WallWidth
  expr: Constraints[11] = <<sheet>>.WallWidth
  expr: Constraints[44] = <<sheet>>.SealWidthTop + 0.1 mm
  expr: Constraints[45] = (<<sheet>>.WallWidth - <<sheet>>.SealWidthTop) / 2
  expr: Constraints[8] = <<sheet>>.WallWidth * 2
  expr: Constraints[9] = <<sheet>>.AntSmallLoraHeight + 1 mm + <<sheet>>.WallWidth * 2
  sketch-geometry (22):
    g0: LineSegment [constr] StartX=-44 StartY=40.1 StartZ=0 EndX=-44 EndY=-42.5 EndZ=0
    g1: LineSegment [constr] StartX=-44 StartY=-42.5 StartZ=0 EndX=44 EndY=-42.5 EndZ=0
    g2: LineSegment [constr] StartX=44 StartY=-42.5 StartZ=0 EndX=44 EndY=40.1 EndZ=0
    g3: LineSegment [constr] StartX=44 StartY=40.1 StartZ=0 EndX=-44 EndY=40.1 EndZ=0
    g4: LineSegment StartX=-45.9 StartY=40.1 StartZ=0 EndX=-45.9 EndY=-42.5 EndZ=0
    g5: LineSegment StartX=-44 StartY=-44.4 StartZ=0 EndX=44 EndY=-44.4 EndZ=0
    g6: LineSegment StartX=45.9 StartY=-42.5 StartZ=0 EndX=45.9 EndY=40.1 EndZ=0
    g7: LineSegment StartX=44 StartY=42 StartZ=0 EndX=-44 EndY=42 EndZ=0
    g8: ArcOfCircle CenterX=-44 CenterY=40.1 CenterZ=0 NormalX=0 NormalY=0 NormalZ=1 AngleXU=0 Radius=1.9 StartAngle=1.5708 EndAngle=3.14159
    g9: ArcOfCircle CenterX=-44 CenterY=-42.5 CenterZ=0 NormalX=0 NormalY=0 NormalZ=1 AngleXU=0 Radius=1.9 StartAngle=3.14159 EndAngle=4.71239
    g10: ArcOfCircle CenterX=44 CenterY=-42.5 CenterZ=0 NormalX=0 NormalY=0 NormalZ=1 AngleXU=0 Radius=1.9 StartAngle=4.71239 EndAngle=6.28319
    g11: ArcOfCircle CenterX=44 CenterY=40.1 CenterZ=0 NormalX=0 NormalY=0 NormalZ=1 AngleXU=0 Radius=1.9 StartAngle=-9e-16 EndAngle=1.5708
    g12: LineSegment StartX=-47.2 StartY=40.1 StartZ=0 EndX=-47.2 EndY=-42.5 EndZ=0
    g13: LineSegment StartX=-44 StartY=-45.7 StartZ=0 EndX=44 EndY=-45.7 EndZ=0
    g14: LineSegment StartX=47.2 StartY=-42.5 StartZ=0 EndX=47.2 EndY=40.1 EndZ=0
    g15: LineSegment StartX=44 StartY=43.3 StartZ=0 EndX=-44 EndY=43.3 EndZ=0
    g16: ArcOfCircle CenterX=-44 CenterY=40.1 CenterZ=0 NormalX=0 NormalY=0 NormalZ=1 AngleXU=0 Radius=3.2 StartAngle=1.5708 EndAngle=3.14159
    g17: ArcOfCircle CenterX=-44 CenterY=-42.5 CenterZ=0 NormalX=0 NormalY=0 NormalZ=1 AngleXU=0 Radius=3.2 StartAngle=3.14159 EndAngle=4.71239
    g18: ArcOfCircle CenterX=44 CenterY=-42.5 CenterZ=0 NormalX=0 NormalY=0 NormalZ=1 AngleXU=0 Radius=3.2 StartAngle=4.71239 EndAngle=6.28319
    g19: ArcOfCircle CenterX=44 CenterY=40.1 CenterZ=0 NormalX=0 NormalY=0 NormalZ=1 AngleXU=0 Radius=3.2 StartAngle=-9e-16 EndAngle=1.5708
    g20: GeomPoint [constr] X=-45.9 Y=42 Z=0
    g21: GeomPoint [constr] X=45.9 Y=-44.4 Z=0
  constraints (49):
    c: Coincident(g0,g1)
    c: Coincident(g1,g2)
    c: Coincident(g2,g3)
    c: Coincident(g3,g0)
    c: Vertical(g0)
    c: Vertical(g2)
    c: Horizontal(g1)
    c: Horizontal(g3)
    c: DistanceY(g-4,g1) = 10
    c: DistanceY(g2,g-3) = 12.4
    c: DistanceX(g1,g-6) = 5
    c: DistanceX(g-5,g0) = 5
    c: Tangent(g4,g8) = -1.5708
    c: Tangent(g4,g9) = -1.5708
    c: Tangent(g5,g9) = -1.5708
    c: Tangent(g5,g10) = -1.5708
    c: Tangent(g6,g10) = -1.5708
    c: Tangent(g6,g11) = -1.5708
    c: Tangent(g7,g11) = -1.5708
    c: Tangent(g7,g8) = -1.5708
    c: Vertical(g4)
    c: Vertical(g6)
    c: Horizontal(g5)
    c: Horizontal(g7)
    c: Equal(g9,g10)
    c: Tangent(g12,g16) = -1.5708
    c: Tangent(g12,g17) = -1.5708
    c: Tangent(g13,g17) = -1.5708
    c: Tangent(g13,g18) = -1.5708
    c: Tangent(g14,g18) = -1.5708
    c: Tangent(g14,g19) = -1.5708
    c: Tangent(g15,g19) = -1.5708
    c: Tangent(g15,g16) = -1.5708
    c: Coincident(g8,g16)
    c: Coincident(g9,g17)
    c: Coincident(g10,g18)
    c: Coincident(g11,g19)
    c: Vertical(g12)
    c: Vertical(g14)
    c: Horizontal(g13)
    c: PointOnObject(g20,g4)
    c: PointOnObject(g20,g7)
    c: PointOnObject(g21,g5)
    c: PointOnObject(g21,g6)
    c: DistanceY(g7,g15) = 1.3
    c: DistanceY(g0,g7) = 1.9
    c: Coincident(g11,g2)
    c: Coincident(g0,g8)
    c: Coincident(g9,g0)
FEATURE [PartDesign::Plane] DatumPlane001  label="SealBottomPlane"
  AttachmentOffset = pos=(0,0,3) rot=(0,0,1;0rad)
  AttachmentSupport = -> [Pad006]
  Length = 120.688
  MapMode = 5
  Placement = pos=(0,0,3.6) rot=(0,0,1;0rad)
  ResizeMode = 0
  Width = 127.688
  expr: .AttachmentOffset.Base.z = <<sheet>>.SealHeight
FEATURE [Sketcher::SketchObject] Sketch010  label="SealBottomSketch"
  ArcFitTolerance = 1e-06
  AttachmentSupport = -> [DatumPlane001]
  ExternalGeometry = -> [Sketch009]
  FullyConstrained = true
  MakeInternals = false
  MapMode = 5
  Placement = pos=(0,0,3.6) rot=(0,0,1;0rad)
  expr: Constraints[36] = <<sheet>>.SealWidthTop - 0.1 mm
  sketch-geometry (18):
    g0: LineSegment StartX=-45.9 StartY=40.1 StartZ=0 EndX=-45.9 EndY=-42.5 EndZ=0
    g1: LineSegment StartX=-44 StartY=-44.4 StartZ=0 EndX=44 EndY=-44.4 EndZ=0
    g2: LineSegment StartX=45.9 StartY=-42.5 StartZ=0 EndX=45.9 EndY=40.1 EndZ=0
    g3: LineSegment StartX=44 StartY=42 StartZ=0 EndX=-44 EndY=42 EndZ=0
    g4: ArcOfCircle CenterX=-44 CenterY=40.1 CenterZ=0 NormalX=0 NormalY=0 NormalZ=1 AngleXU=0 Radius=1.9 StartAngle=1.5708 EndAngle=3.14159
    g5: ArcOfCircle CenterX=-44 CenterY=-42.5 CenterZ=0 NormalX=0 NormalY=0 NormalZ=1 AngleXU=0 Radius=1.9 StartAngle=3.14159 EndAngle=4.71239
    g6: ArcOfCircle CenterX=44 CenterY=-42.5 CenterZ=0 NormalX=0 NormalY=0 NormalZ=1 AngleXU=0 Radius=1.9 StartAngle=4.71239 EndAngle=6.28319
    g7: ArcOfCircle CenterX=44 CenterY=40.1 CenterZ=0 NormalX=0 NormalY=0 NormalZ=1 AngleXU=0 Radius=1.9 StartAngle=-6.75e-14 EndAngle=1.5708
    g8: LineSegment StartX=-47 StartY=40.1 StartZ=0 EndX=-47 EndY=-42.5 EndZ=0
    g9: LineSegment StartX=-44 StartY=-45.5 StartZ=0 EndX=44 EndY=-45.5 EndZ=0
    g10: LineSegment StartX=47 StartY=-42.5 StartZ=0 EndX=47 EndY=40.1 EndZ=0
    g11: LineSegment StartX=44 StartY=43.1 StartZ=0 EndX=-44 EndY=43.1 EndZ=0
    g12: ArcOfCircle CenterX=-44 CenterY=40.1 CenterZ=0 NormalX=0 NormalY=0 NormalZ=1 AngleXU=0 Radius=3 StartAngle=1.5708 EndAngle=3.14159
    g13: ArcOfCircle CenterX=-44 CenterY=-42.5 CenterZ=0 NormalX=0 NormalY=0 NormalZ=1 AngleXU=0 Radius=3 StartAngle=3.14159 EndAngle=4.71239
    g14: ArcOfCircle CenterX=44 CenterY=-42.5 CenterZ=0 NormalX=0 NormalY=0 NormalZ=1 AngleXU=0 Radius=3 StartAngle=4.71239 EndAngle=6.28319
    g15: ArcOfCircle CenterX=44 CenterY=40.1 CenterZ=0 NormalX=0 NormalY=0 NormalZ=1 AngleXU=0 Radius=3 StartAngle=8.12e-14 EndAngle=1.5708
    g16: GeomPoint [constr] X=-45.9 Y=42 Z=0
    g17: GeomPoint [constr] X=45.9 Y=-44.4 Z=0
  constraints (37):
    c: Tangent(g0,g4) = -1.5708
    c: Tangent(g0,g5) = -1.5708
    c: Tangent(g1,g5) = -1.5708
    c: Tangent(g1,g6) = -1.5708
    c: Tangent(g2,g6) = -1.5708
    c: Tangent(g2,g7) = -1.5708
    c: Tangent(g3,g7) = -1.5708
    c: Tangent(g3,g4) = -1.5708
    c: Vertical(g0)
    c: Vertical(g2)
    c: Horizontal(g1)
    c: Equal(g4,g5)
    c: Equal(g5,g6)
    c: Equal(g6,g7)
    c: Tangent(g8,g12) = -1.5708
    c: Tangent(g8,g13) = -1.5708
    c: Tangent(g9,g13) = -1.5708
    c: Tangent(g9,g14) = -1.5708
    c: Tangent(g10,g14) = -1.5708
    c: Tangent(g10,g15) = -1.5708
    c: Tangent(g11,g15) = -1.5708
    c: Tangent(g11,g12) = -1.5708
    c: Coincident(g4,g12)
    c: Coincident(g5,g13)
    c: Coincident(g6,g14)
    c: Coincident(g7,g15)
    c: Vertical(g8)
    c: Vertical(g10)
    c: Horizontal(g9)
    c: PointOnObject(g16,g0)
    c: PointOnObject(g16,g3)
    c: PointOnObject(g17,g1)
    c: PointOnObject(g17,g2)
    c: Coincident(g2,g-3)
    c: Coincident(g3,g-4)
    c: Coincident(g3,g-4)
    c: DistanceY(g3,g11) = 1.1
FEATURE [PartDesign::AdditiveLoft] AdditiveLoft  label="SealSeal"
  BaseFeature = -> Pad006
  Closed = false
  Profile = -> Sketch009
  Ruled = false
  Sections = -> [Sketch010]
  Suppressed = false
FEATURE [PartDesign::SubShapeBinder] Binder  label="SealBoxBinder"
  BindCopyOnChange = 0
  BindMode = 0
  ClaimChildren = false
  Context = -> Body001 [Binder.]
  Fuse = false
  MakeFace = true
  OffsetFill = false
  OffsetIntersection = false
  OffsetJoinType = 0
  OffsetOpenResult = false
  PartialLoad = false
  Relative = true
  Support = -> [Body[Pocket001.]]
  _Version = 2
FEATURE [Sketcher::SketchObject] Sketch011  label="SealBoxLidHolesSketch"
  ArcFitTolerance = 1e-06
  AttachmentSupport = -> [XY_Plane001]
  ExternalGeometry = -> [Binder]
  FullyConstrained = true
  MakeInternals = false
  MapMode = 5
  sketch-geometry (7):
    g0: Circle CenterX=-44 CenterY=-49.1667 CenterZ=0 NormalX=0 NormalY=0 NormalZ=1 AngleXU=0 Radius=1.5
    g1: Circle CenterX=-29 CenterY=-49.1667 CenterZ=0 NormalX=0 NormalY=0 NormalZ=1 AngleXU=0 Radius=1.5
    g2: Circle CenterX=31 CenterY=-49.1667 CenterZ=0 NormalX=0 NormalY=0 NormalZ=1 AngleXU=0 Radius=1.5
    g3: Circle CenterX=-29 CenterY=46.7667 CenterZ=0 NormalX=0 NormalY=0 NormalZ=1 AngleXU=0 Radius=1.5
    g4: Circle CenterX=31 CenterY=46.7667 CenterZ=0 NormalX=0 NormalY=0 NormalZ=1 AngleXU=0 Radius=1.5
    g5: Circle CenterX=44 CenterY=46.7667 CenterZ=0 NormalX=0 NormalY=0 NormalZ=1 AngleXU=0 Radius=1.5
    g6: Circle CenterX=44 CenterY=-49.1667 CenterZ=0 NormalX=0 NormalY=0 NormalZ=1 AngleXU=0 Radius=1.5
  constraints (14):
    c: Diameter(g0) = 3
    c: Equal(g0,g1)
    c: Equal(g1,g2)
    c: Equal(g2,g6)
    c: Equal(g6,g5)
    c: Equal(g5,g4)
    c: Equal(g4,g3)
    c: Coincident(g6,g-8)
    c: Coincident(g2,g-9)
    c: Coincident(g1,g-3)
    c: Coincident(g0,g-4)
    c: Coincident(g3,g-5)
    c: Coincident(g4,g-6)
    c: Coincident(g5,g-7)
FEATURE [PartDesign::Pocket] Pocket002  label="SealBoxLidHoles"
  BaseFeature = -> AdditiveLoft
  Direction = (0,0,-1)
  Length = 0.6
  Length2 = 5
  Profile = -> Sketch011
  ReferenceAxis = -> Sketch011 [N_Axis]
  Reversed = true
  Suppressed = false
  Type = 0
  expr: Length = <<SealBase>>.Length
FEATURE [Sketcher::SketchObject] Sketch012  label="SealInnserSealSketch"
  ArcFitTolerance = 1e-06
  AttachmentSupport = -> [XY_Plane001]
  ExternalGeometry = -> [Binder]
  FullyConstrained = true
  MakeInternals = false
  MapMode = 5
  expr: Constraints[10] = <<sheet>>.SealWidthTop
  expr: Constraints[11] = <<sheet>>.SealWidthTop
  expr: Constraints[12] = <<sheet>>.SealWidthTop
  expr: Constraints[45] = <<sheet>>.SealWidthTop
  expr: Constraints[59] = <<sheet>>.SealWidthTop
  expr: Constraints[60] = <<sheet>>.SealWidthTop
  expr: Constraints[61] = <<sheet>>.BatteryMountDistance
  expr: Constraints[64] = <<sheet>>.SealWidthTop
  expr: Constraints[65] = <<sheet>>.BatteryWidth
  sketch-geometry (24):
    g0: LineSegment StartX=44 StartY=40.1 StartZ=0 EndX=44 EndY=-24.5 EndZ=0
    g1: LineSegment StartX=-44 StartY=-24.5 StartZ=0 EndX=-44 EndY=40.1 EndZ=0
    g2: LineSegment StartX=-42.8 StartY=38.9 StartZ=0 EndX=42.8 EndY=38.9 EndZ=0
    g3: LineSegment StartX=42.8 StartY=38.9 StartZ=0 EndX=42.8 EndY=-23.3 EndZ=0
    g4: LineSegment StartX=36.3 StartY=-23.3 StartZ=0 EndX=36.3 EndY=-41.3 EndZ=0
    g5: LineSegment StartX=36.3 StartY=-41.3 StartZ=0 EndX=-36.3 EndY=-41.3 EndZ=0
    g6: LineSegment StartX=-36.3 StartY=-41.3 StartZ=0 EndX=-36.3 EndY=-23.3 EndZ=0
    g7: LineSegment StartX=-42.8 StartY=38.9 StartZ=0 EndX=-42.8 EndY=-23.3 EndZ=0
    g8: LineSegment StartX=-44 StartY=40.1 StartZ=0 EndX=-41 EndY=40.1 EndZ=0
    g9: LineSegment StartX=-41 StartY=40.1 StartZ=0 EndX=-41 EndY=43.5 EndZ=0
    g10: LineSegment StartX=-41 StartY=43.5 StartZ=0 EndX=-39.5 EndY=43.5 EndZ=0
    g11: LineSegment StartX=-39.5 StartY=43.5 StartZ=0 EndX=-39.5 EndY=40.1 EndZ=0
    g12: LineSegment StartX=-39.5 StartY=40.1 StartZ=0 EndX=7.05 EndY=40.1 EndZ=0
    g13: LineSegment StartX=7.05 StartY=40.1 StartZ=0 EndX=7.05 EndY=49.35 EndZ=0
    g14: LineSegment StartX=7.05 StartY=49.35 StartZ=0 EndX=8.45 EndY=49.35 EndZ=0
    g15: LineSegment StartX=8.45 StartY=49.35 StartZ=0 EndX=8.45 EndY=40.1 EndZ=0
    g16: LineSegment StartX=44 StartY=40.1 StartZ=0 EndX=8.45 EndY=40.1 EndZ=0
    g17: LineSegment StartX=-37.5 StartY=-24.5 StartZ=0 EndX=-37.5 EndY=-42.5 EndZ=0
    g18: LineSegment StartX=-37.5 StartY=-42.5 StartZ=0 EndX=37.5 EndY=-42.5 EndZ=0
    g19: LineSegment StartX=37.5 StartY=-42.5 StartZ=0 EndX=37.5 EndY=-24.5 EndZ=0
    g20: LineSegment StartX=-36.3 StartY=-23.3 StartZ=0 EndX=-42.8 EndY=-23.3 EndZ=0
    g21: LineSegment StartX=-44 StartY=-24.5 StartZ=0 EndX=-37.5 EndY=-24.5 EndZ=0
    g22: LineSegment StartX=36.3 StartY=-23.3 StartZ=0 EndX=42.8 EndY=-23.3 EndZ=0
    g23: LineSegment StartX=37.5 StartY=-24.5 StartZ=0 EndX=44 EndY=-24.5 EndZ=0
  constraints (66):
    c: Horizontal(g2)
    c: Coincident(g3,g2)
    c: Vertical(g3)
    c: Coincident(g5,g4)
    c: Horizontal(g5)
    c: Coincident(g6,g5)
    c: Coincident(g7,g2)
    c: Vertical(g7)
    c: Vertical(g4)
    c: Vertical(g6)
    c: DistanceY(g2,g-3) = 1.2
    c: DistanceX(g3,g0) = 1.2
    c: DistanceY(g0,g3) = 1.2
    c: Coincident(g1,g8)
    c: Horizontal(g8)
    c: Coincident(g8,g9)
    c: Coincident(g9,g-5)
    c: Vertical(g9)
    c: Coincident(g9,g10)
    c: Coincident(g10,g-8)
    c: Coincident(g10,g11)
    c: Vertical(g11)
    c: Vertical(g0)
    c: Horizontal(g8,g11)
    c: Coincident(g1,g-3)
    c: Coincident(g12,g11)
    c: Horizontal(g12)
    c: Coincident(g13,g12)
    c: Vertical(g13)
    c: Coincident(g14,g13)
    c: Horizontal(g14)
    c: Coincident(g15,g14)
    c: Vertical(g15)
    c: Coincident(g16,g0)
    c: Coincident(g16,g15)
    c: Horizontal(g16)
    c: Horizontal(g15,g12)
    c: Horizontal(g13,g-6)
    c: DistanceX(g-6,g13) = 0.05
    c: Distance(g14,g-7) = 0.05
    c: Coincident(g18,g17)
    c: Horizontal(g18)
    c: Coincident(g19,g18)
    c: Vertical(g19)
    c: Vertical(g17)
    c: DistanceY(g17,g5) = 1.2
    c: Coincident(g20,g6)
    c: Coincident(g20,g7)
    c: Horizontal(g20)
    c: Coincident(g21,g1)
    c: Coincident(g21,g17)
    c: Horizontal(g21)
    c: Coincident(g22,g4)
    c: Coincident(g22,g3)
    c: Horizontal(g22)
    c: Coincident(g23,g19)
    c: Coincident(g23,g0)
    c: Horizontal(g23)
    c: Symmetric(g6,g4,g-2)
    c: DistanceX(g17,g6) = 1.2
    c: DistanceX(g4,g19) = 1.2
    c: DistanceX(g17,g19) = 75
    c: Coincident(g1,g-3)
    c: Coincident(g0,g-4)
    c: DistanceX(g1,g7) = 1.2
    c: DistanceY(g4,g4) = 18
FEATURE [PartDesign::Pad] Pad007  label="SealInnerSeal"
  BaseFeature = -> Pocket002
  Direction = (0,0,1)
  Length = 3.6
  Length2 = 10
  Profile = -> Sketch012
  ReferenceAxis = -> Sketch012 [N_Axis]
  Suppressed = false
  Type = 0
  expr: Length = <<sheet>>.SealHeight + <<SealBase>>.Length
FEATURE [PartDesign::SubShapeBinder] Binder001  label="LidBoxBinder"
  BindCopyOnChange = 0
  BindMode = 0
  ClaimChildren = false
  Context = -> Body002 [Binder001.]
  Fuse = false
  MakeFace = true
  OffsetFill = false
  OffsetIntersection = false
  OffsetJoinType = 0
  OffsetOpenResult = false
  PartialLoad = false
  Relative = true
  Support = -> [Body[Pocket001.]]
  _Version = 2
FEATURE [Sketcher::SketchObject] Sketch013  label="LidBaseSketch"
  ArcFitTolerance = 1e-06
  AttachmentSupport = -> [XY_Plane002]
  ExternalGeometry = -> [Binder001]
  FullyConstrained = true
  MakeInternals = false
  MapMode = 5
  expr: Constraints[33] = <<sheet>>.SealOuterWidth
  expr: Constraints[34] = <<sheet>>.SealOuterWidth
  expr: Constraints[35] = <<sheet>>.BoxCornerRadius
  expr: Constraints[36] = <<sheet>>.SealOuterWidth
  expr: Constraints[37] = <<sheet>>.SealOuterWidth
  sketch-geometry (17):
    g0: Circle CenterX=-44 CenterY=46.7667 CenterZ=0 NormalX=0 NormalY=0 NormalZ=1 AngleXU=0 Radius=1.65
    g1: Circle CenterX=-31 CenterY=46.7667 CenterZ=0 NormalX=0 NormalY=0 NormalZ=1 AngleXU=0 Radius=1.65
    g2: Circle CenterX=29 CenterY=46.7667 CenterZ=0 NormalX=0 NormalY=0 NormalZ=1 AngleXU=0 Radius=1.65
    g3: Circle CenterX=44 CenterY=-49.1667 CenterZ=0 NormalX=0 NormalY=0 NormalZ=1 AngleXU=0 Radius=1.65
    g4: Circle CenterX=29 CenterY=-49.1667 CenterZ=0 NormalX=0 NormalY=0 NormalZ=1 AngleXU=0 Radius=1.65
    g5: Circle CenterX=-31 CenterY=-49.1667 CenterZ=0 NormalX=0 NormalY=0 NormalZ=1 AngleXU=0 Radius=1.65
    g6: Circle CenterX=-44 CenterY=-49.1667 CenterZ=0 NormalX=0 NormalY=0 NormalZ=1 AngleXU=0 Radius=1.65
    g7: LineSegment StartX=-50 StartY=52 StartZ=0 EndX=-50 EndY=-52 EndZ=0
    g8: LineSegment StartX=-48.5 StartY=-53.5 StartZ=0 EndX=48.5 EndY=-53.5 EndZ=0
    g9: LineSegment StartX=50 StartY=-52 StartZ=0 EndX=50 EndY=52 EndZ=0
    g10: LineSegment StartX=48.5 StartY=53.5 StartZ=0 EndX=-48.5 EndY=53.5 EndZ=0
    g11: ArcOfCircle CenterX=-48.5 CenterY=52 CenterZ=0 NormalX=0 NormalY=0 NormalZ=1 AngleXU=0 Radius=1.5 StartAngle=1.5708 EndAngle=3.14159
    g12: ArcOfCircle CenterX=-48.5 CenterY=-52 CenterZ=0 NormalX=0 NormalY=0 NormalZ=1 AngleXU=0 Radius=1.5 StartAngle=3.14159 EndAngle=4.71239
    g13: ArcOfCircle CenterX=48.5 CenterY=-52 CenterZ=0 NormalX=0 NormalY=0 NormalZ=1 AngleXU=0 Radius=1.5 StartAngle=4.71239 EndAngle=6.28319
    g14: ArcOfCircle CenterX=48.5 CenterY=52 CenterZ=0 NormalX=0 NormalY=0 NormalZ=1 AngleXU=0 Radius=1.5 StartAngle=-9e-16 EndAngle=1.5708
    g15: GeomPoint [constr] X=-50 Y=53.5 Z=0
    g16: GeomPoint [constr] X=50 Y=-53.5 Z=0
  constraints (38):
    c: Coincident(g0,g-4)
    c: Coincident(g1,g-5)
    c: Coincident(g2,g-6)
    c: Coincident(g3,g-8)
    c: Coincident(g4,g-7)
    c: Coincident(g5,g-10)
    c: Coincident(g6,g-9)
    c: Diameter(g0) = 3.3
    c: Equal(g0,g1)
    c: Equal(g1,g2)
    c: Equal(g2,g6)
    c: Equal(g6,g5)
    c: Equal(g5,g4)
    c: Equal(g4,g3)
    c: Tangent(g7,g11) = -1.5708
    c: Tangent(g7,g12) = -1.5708
    c: Tangent(g8,g12) = -1.5708
    c: Tangent(g8,g13) = -1.5708
    c: Tangent(g9,g13) = -1.5708
    c: Tangent(g9,g14) = -1.5708
    c: Tangent(g10,g14) = -1.5708
    c: Tangent(g10,g11) = -1.5708
    c: Vertical(g7)
    c: Vertical(g9)
    c: Horizontal(g8)
    c: Horizontal(g10)
    c: Equal(g11,g12)
    c: Equal(g12,g13)
    c: Equal(g13,g14)
    c: PointOnObject(g15,g7)
    c: PointOnObject(g15,g10)
    c: PointOnObject(g16,g8)
    c: PointOnObject(g16,g9)
    c: DistanceY(g-3,g10) = 1
    c: DistanceX(g-13,g9) = 1
    c: Radius(g14) = 1.5
    c: DistanceX(g7,g-11) = 1
    c: DistanceY(g8,g-12) = 1
FEATURE [PartDesign::Pad] Pad008  label="LidBase"
  Direction = (0,0,1)
  Length = 1
  Length2 = 10
  Profile = -> Sketch013
  ReferenceAxis = -> Sketch013 [N_Axis]
  Suppressed = false
  Type = 0
  expr: Length = <<sheet>>.WallBottomThickness
FEATURE [PartDesign::SubShapeBinder] Binder002  label="StrapBoxBinder"
  BindCopyOnChange = 0
  BindMode = 0
  ClaimChildren = false
  Context = -> Body003 [Binder002.]
  Fuse = false
  MakeFace = true
  OffsetFill = false
  OffsetIntersection = false
  OffsetJoinType = 0
  OffsetOpenResult = false
  PartialLoad = false
  Relative = true
  Support = -> [Body[Pocket001.]]
  _Version = 2
FEATURE [Sketcher::SketchObject] Sketch014  label="StrapBaseSketch"
  ArcFitTolerance = 1e-06
  AttachmentSupport = -> [XY_Plane003]
  ExternalGeometry = -> [Binder002]
  FullyConstrained = true
  MakeInternals = false
  MapMode = 5
  sketch-geometry (10):
    g0: LineSegment StartX=-49 StartY=51 StartZ=0 EndX=-49 EndY=-51 EndZ=0
    g1: LineSegment StartX=-47.5 StartY=-52.5 StartZ=0 EndX=47.5 EndY=-52.5 EndZ=0
    g2: LineSegment StartX=49 StartY=-51 StartZ=0 EndX=49 EndY=51 EndZ=0
    g3: LineSegment StartX=47.5 StartY=52.5 StartZ=0 EndX=-47.5 EndY=52.5 EndZ=0
    g4: ArcOfCircle CenterX=-47.5 CenterY=51 CenterZ=0 NormalX=0 NormalY=0 NormalZ=1 AngleXU=0 Radius=1.5 StartAngle=1.5708 EndAngle=3.14159
    g5: ArcOfCircle CenterX=-47.5 CenterY=-51 CenterZ=0 NormalX=0 NormalY=0 NormalZ=1 AngleXU=0 Radius=1.5 StartAngle=3.14159 EndAngle=4.71239
    g6: ArcOfCircle CenterX=47.5 CenterY=-51 CenterZ=0 NormalX=0 NormalY=0 NormalZ=1 AngleXU=0 Radius=1.5 StartAngle=4.71239 EndAngle=6.28319
    g7: ArcOfCircle CenterX=47.5 CenterY=51 CenterZ=0 NormalX=0 NormalY=0 NormalZ=1 AngleXU=0 Radius=1.5 StartAngle=7.728e-13 EndAngle=1.5708
    g8: GeomPoint [constr] X=-49 Y=52.5 Z=0
    g9: GeomPoint [constr] X=49 Y=-52.5 Z=0
  constraints (21):
    c: Tangent(g0,g4) = -1.5708
    c: Tangent(g0,g5) = -1.5708
    c: Tangent(g1,g5) = -1.5708
    c: Tangent(g1,g6) = -1.5708
    c: Tangent(g2,g6) = -1.5708
    c: Tangent(g2,g7) = -1.5708
    c: Tangent(g3,g7) = -1.5708
    c: Tangent(g3,g4) = -1.5708
    c: Vertical(g0)
    c: Vertical(g2)
    c: Horizontal(g1)
    c: Horizontal(g3)
    c: Equal(g5,g6)
    c: Equal(g6,g7)
    c: PointOnObject(g8,g0)
    c: PointOnObject(g8,g3)
    c: PointOnObject(g9,g1)
    c: PointOnObject(g9,g2)
    c: Coincident(g-3,g3)
    c: Coincident(g2,g-4)
    c: Coincident(g1,g-5)
FEATURE [PartDesign::Pad] Pad009  label="StrapBase"
  Direction = (0,0,1)
  Length = 1.4
  Length2 = 10
  Profile = -> Sketch014
  ReferenceAxis = -> Sketch014 [N_Axis]
  Reversed = true
  Suppressed = false
  Type = 0
FEATURE [Sketcher::SketchObject] Sketch015
  ArcFitTolerance = 1e-06
  AttachmentSupport = -> [XY_Plane003]
  ExternalGeometry = -> [Binder002]
  FullyConstrained = true
  MakeInternals = false
  MapMode = 5
  sketch-geometry (7):
    g0: Circle CenterX=-44 CenterY=46.7667 CenterZ=0 NormalX=0 NormalY=0 NormalZ=1 AngleXU=0 Radius=3.25
    g1: Circle CenterX=-31 CenterY=46.7667 CenterZ=0 NormalX=0 NormalY=0 NormalZ=1 AngleXU=0 Radius=3.25
    g2: Circle CenterX=29 CenterY=46.7667 CenterZ=0 NormalX=0 NormalY=0 NormalZ=1 AngleXU=0 Radius=3.25
    g3: Circle CenterX=-44 CenterY=-49.1667 CenterZ=0 NormalX=0 NormalY=0 NormalZ=1 AngleXU=0 Radius=3.25
    g4: Circle CenterX=-31 CenterY=-49.1667 CenterZ=0 NormalX=0 NormalY=0 NormalZ=1 AngleXU=0 Radius=3.25
    g5: Circle CenterX=29 CenterY=-49.1667 CenterZ=0 NormalX=0 NormalY=0 NormalZ=1 AngleXU=0 Radius=3.25
    g6: Circle CenterX=44 CenterY=-49.1667 CenterZ=0 NormalX=0 NormalY=0 NormalZ=1 AngleXU=0 Radius=3.25
  constraints (14):
    c: Coincident(g0,g-3)
    c: Coincident(g1,g-4)
    c: Coincident(g2,g-5)
    c: Coincident(g3,g-9)
    c: Coincident(g4,g-8)
    c: Coincident(g5,g-7)
    c: Coincident(g6,g-6)
    c: Diameter(g0) = 6.5
    c: Equal(g0,g1)
    c: Equal(g1,g2)
    c: Equal(g2,g3)
    c: Equal(g3,g4)
    c: Equal(g4,g5)
    c: Equal(g5,g6)
FEATURE [PartDesign::Pad] Pad010
  BaseFeature = -> Pad009
  Direction = (0,0,1)
  Length = 2.7
  Length2 = 10
  Profile = -> Sketch015
  ReferenceAxis = -> Sketch015 [N_Axis]
  Reversed = true
  Suppressed = false
  Type = 0
FEATURE [PartDesign::Hole] Hole
  BaseFeature = -> Pad010
  CustomThreadClearance = 0
  Depth = 25
  DepthType = 0
  Diameter = 3.4
  DrillForDepth = false
  DrillPoint = 1
  DrillPointAngle = 118
  HoleCutCountersinkAngle = 90
  HoleCutCustomValues = false
  HoleCutDepth = 0
  HoleCutDiameter = 6.1
  HoleCutType = 2
  ModelThread = false
  Profile = -> Sketch015
  Suppressed = false
  Tapered = false
  TaperedAngle = 90
  ThreadClass = 0
  ThreadDepth = 25
  ThreadDepthType = 0
  ThreadDirection = 0
  ThreadFit = 0
  ThreadSize = 9
  ThreadType = 2
  Threaded = false
  UseCustomThreadClearance = false
FEATURE [Sketcher::SketchObject] Sketch016
  ArcFitTolerance = 1e-06
  AttachmentSupport = -> [Hole]
  FullyConstrained = true
  MakeInternals = false
  MapMode = 5
  sketch-geometry (16):
    g0: ArcOfCircle CenterX=-25 CenterY=35 CenterZ=0 NormalX=0 NormalY=0 NormalZ=1 AngleXU=0 Radius=2 StartAngle=1.5708 EndAngle=4.71239
    g1: ArcOfCircle CenterX=25 CenterY=35 CenterZ=0 NormalX=0 NormalY=0 NormalZ=1 AngleXU=0 Radius=2 StartAngle=4.71239 EndAngle=7.85398
    g2: LineSegment StartX=-25 StartY=37 StartZ=0 EndX=25 EndY=37 EndZ=0
    g3: LineSegment StartX=-25 StartY=33 StartZ=0 EndX=25 EndY=33 EndZ=0
    g4: ArcOfCircle CenterX=-25 CenterY=-35 CenterZ=0 NormalX=0 NormalY=0 NormalZ=1 AngleXU=0 Radius=2 StartAngle=1.5708 EndAngle=4.71239
    g5: ArcOfCircle CenterX=25 CenterY=-35 CenterZ=0 NormalX=0 NormalY=0 NormalZ=1 AngleXU=0 Radius=2 StartAngle=4.71239 EndAngle=7.85398
    g6: LineSegment StartX=-25 StartY=-33 StartZ=0 EndX=25 EndY=-33 EndZ=0
    g7: LineSegment StartX=-25 StartY=-37 StartZ=0 EndX=25 EndY=-37 EndZ=0
    g8: ArcOfCircle CenterX=-25 CenterY=20 CenterZ=0 NormalX=0 NormalY=0 NormalZ=1 AngleXU=0 Radius=2 StartAngle=1.5708 EndAngle=4.71239
    g9: ArcOfCircle CenterX=25 CenterY=20 CenterZ=0 NormalX=0 NormalY=0 NormalZ=1 AngleXU=0 Radius=2 StartAngle=4.71239 EndAngle=7.85398
    g10: LineSegment StartX=-25 StartY=22 StartZ=0 EndX=25 EndY=22 EndZ=0
    g11: LineSegment StartX=-25 StartY=18 StartZ=0 EndX=25 EndY=18 EndZ=0
    g12: ArcOfCircle CenterX=-25 CenterY=-20 CenterZ=0 NormalX=0 NormalY=0 NormalZ=1 AngleXU=0 Radius=2 StartAngle=1.5708 EndAngle=4.71239
    g13: ArcOfCircle CenterX=25 CenterY=-20 CenterZ=0 NormalX=0 NormalY=0 NormalZ=1 AngleXU=0 Radius=2 StartAngle=4.71239 EndAngle=7.85398
    g14: LineSegment StartX=-25 StartY=-18 StartZ=0 EndX=25 EndY=-18 EndZ=0
    g15: LineSegment StartX=-25 StartY=-22 StartZ=0 EndX=25 EndY=-22 EndZ=0
  constraints (38):
    c: Tangent(g0,g2) = 1.5708
    c: Tangent(g0,g3) = -1.5708
    c: Tangent(g1,g2) = 1.5708
    c: Tangent(g1,g3) = -1.5708
    c: Equal(g0,g1)
    c: Tangent(g4,g6) = 1.5708
    c: Tangent(g4,g7) = -1.5708
    c: Tangent(g5,g6) = 1.5708
    c: Tangent(g5,g7) = -1.5708
    c: Equal(g4,g5)
    c: Symmetric(g1,g0,g-2)
    c: Symmetric(g5,g4,g-2)
    c: DistanceX(g0,g1) = 50
    c: Vertical(g0,g4)
    c: Distance(g1,g1) = 4
    c: DistanceY(g5,g5) = 4
    c: Tangent(g8,g10) = 1.5708
    c: Tangent(g8,g11) = -1.5708
    c: Tangent(g9,g10) = 1.5708
    c: Tangent(g9,g11) = -1.5708
    c: Equal(g8,g9)
    c: Horizontal(g10)
    c: Tangent(g12,g14) = 1.5708
    c: Tangent(g12,g15) = -1.5708
    c: Tangent(g13,g14) = 1.5708
    c: Tangent(g13,g15) = -1.5708
    c: Equal(g12,g13)
    c: Horizontal(g14)
    c: Vertical(g1,g9)
    c: Vertical(g9,g13)
    c: Vertical(g8,g12)
    c: Vertical(g0,g8)
    c: DistanceY(g9,g9) = 4
    c: DistanceY(g13,g13) = 4
    c: DistanceY(g12,g-1) = 20
    c: DistanceY(g-1,g8) = 20
    c: DistanceY(g-1,g0) = 35
    c: DistanceY(g4,g-1) = 35
FEATURE [PartDesign::Pocket] Pocket003
  BaseFeature = -> Hole
  Direction = (0,0,-1)
  Length = 1.4
  Length2 = 5
  Profile = -> Sketch016
  ReferenceAxis = -> Sketch016 [N_Axis]
  Suppressed = false
  Type = 0
  expr: Length = <<StrapBase>>.Length
FEATURE [PartDesign::Body] Body003  label="Strap"
  AllowCompound = false
  Group = -> [Sketch014,Binder002,Pad009,Sketch015,Pad010,Hole,Sketch016,Pocket003]
  Origin = -> Origin003
  Placement = pos=(0,0,63.5) rot=(0,0,1;0rad)
  Tip = -> Pocket003
FEATURE [Sketcher::SketchObject] Sketch018
  ArcFitTolerance = 1e-06
  AttachmentOffset = pos=(0,0,1) rot=(0,0,1;0rad)
  AttachmentSupport = -> [XY_Plane002]
  ExternalGeometry = -> [Sketch013]
  FullyConstrained = true
  MakeInternals = false
  MapMode = 5
  Placement = pos=(0,0,1) rot=(0,0,1;0rad)
  expr: Constraints[33] = <<sheet>>.SealOuterWidth
  sketch-geometry (18):
    g0: LineSegment StartX=-50 StartY=52 StartZ=0 EndX=-50 EndY=-52 EndZ=0
    g1: LineSegment StartX=-48.5 StartY=-53.5 StartZ=0 EndX=48.5 EndY=-53.5 EndZ=0
    g2: LineSegment StartX=50 StartY=-52 StartZ=0 EndX=50 EndY=52 EndZ=0
    g3: LineSegment StartX=48.5 StartY=53.5 StartZ=0 EndX=-48.5 EndY=53.5 EndZ=0
    g4: ArcOfCircle CenterX=-48.5 CenterY=52 CenterZ=0 NormalX=0 NormalY=0 NormalZ=1 AngleXU=0 Radius=1.5 StartAngle=1.5708 EndAngle=3.14159
    g5: ArcOfCircle CenterX=-48.5 CenterY=-52 CenterZ=0 NormalX=0 NormalY=0 NormalZ=1 AngleXU=0 Radius=1.5 StartAngle=3.14159 EndAngle=4.71239
    g6: ArcOfCircle CenterX=48.5 CenterY=-52 CenterZ=0 NormalX=0 NormalY=0 NormalZ=1 AngleXU=0 Radius=1.5 StartAngle=4.71239 EndAngle=6.28319
    g7: ArcOfCircle CenterX=48.5 CenterY=52 CenterZ=0 NormalX=0 NormalY=0 NormalZ=1 AngleXU=0 Radius=1.5 StartAngle=-4.3041e-12 EndAngle=1.5708
    g8: LineSegment StartX=-51 StartY=52 StartZ=0 EndX=-51 EndY=-52 EndZ=0
    g9: LineSegment StartX=-48.5 StartY=-54.5 StartZ=0 EndX=48.5 EndY=-54.5 EndZ=0
    g10: LineSegment StartX=51 StartY=-52 StartZ=0 EndX=51 EndY=52 EndZ=0
    g11: LineSegment StartX=48.5 StartY=54.5 StartZ=0 EndX=-48.5 EndY=54.5 EndZ=0
    g12: ArcOfCircle CenterX=-48.5 CenterY=52 CenterZ=0 NormalX=0 NormalY=0 NormalZ=1 AngleXU=0 Radius=2.5 StartAngle=1.5708 EndAngle=3.14159
    g13: ArcOfCircle CenterX=-48.5 CenterY=-52 CenterZ=0 NormalX=0 NormalY=0 NormalZ=1 AngleXU=0 Radius=2.5 StartAngle=3.14159 EndAngle=4.71239
    g14: ArcOfCircle CenterX=48.5 CenterY=-52 CenterZ=0 NormalX=0 NormalY=0 NormalZ=1 AngleXU=0 Radius=2.5 StartAngle=4.71239 EndAngle=6.28319
    g15: ArcOfCircle CenterX=48.5 CenterY=52 CenterZ=0 NormalX=0 NormalY=0 NormalZ=1 AngleXU=0 Radius=2.5 StartAngle=-1.51e-13 EndAngle=1.5708
    g16: GeomPoint [constr] X=-50 Y=53.5 Z=0
    g17: GeomPoint [constr] X=50 Y=-53.5 Z=0
  constraints (36):
    c: Tangent(g0,g4) = -1.5708
    c: Tangent(g0,g5) = -1.5708
    c: Tangent(g1,g5) = -1.5708
    c: Tangent(g1,g6) = -1.5708
    c: Tangent(g2,g6) = -1.5708
    c: Tangent(g2,g7) = -1.5708
    c: Tangent(g3,g7) = -1.5708
    c: Tangent(g3,g4) = -1.5708
    c: Vertical(g2)
    c: Horizontal(g1)
    c: Equal(g5,g6)
    c: Equal(g6,g7)
    c: Tangent(g8,g12) = -1.5708
    c: Tangent(g8,g13) = -1.5708
    c: Tangent(g9,g13) = -1.5708
    c: Tangent(g9,g14) = -1.5708
    c: Tangent(g10,g14) = -1.5708
    c: Tangent(g10,g15) = -1.5708
    c: Tangent(g11,g15) = -1.5708
    c: Tangent(g11,g12) = -1.5708
    c: Coincident(g4,g12)
    c: Coincident(g5,g13)
    c: Coincident(g6,g14)
    c: Coincident(g7,g15)
    c: Vertical(g8)
    c: Vertical(g10)
    c: Horizontal(g9)
    c: PointOnObject(g16,g0)
    c: PointOnObject(g16,g3)
    c: PointOnObject(g17,g1)
    c: PointOnObject(g17,g2)
    c: Coincident(g-3,g3)
    c: Coincident(g3,g-3)
    c: DistanceY(g3,g11) = 1
    c: Coincident(g0,g-5)
    c: Coincident(g-4,g1)
FEATURE [PartDesign::Pad] Pad012
  BaseFeature = -> Pad008
  Direction = (0,0,1)
  Length = 5
  Length2 = 10
  Profile = -> Sketch018
  ReferenceAxis = -> Sketch018 [N_Axis]
  Reversed = true
  Suppressed = false
  Type = 0
FEATURE [PartDesign::Body] Body002  label="Lid"
  AllowCompound = false
  Group = -> [Binder001,Sketch013,Pad008,Sketch018,Pad012]
  Origin = -> Origin002
  Placement = pos=(0,0,42.5) rot=(0,0,1;0rad)
  Tip = -> Pad012
FEATURE [Sketcher::SketchObject] Sketch019  label="SealOuterwallSketch"
  ArcFitTolerance = 1e-06
  AttachmentSupport = -> [XY_Plane001]
  ExternalGeometry = -> [Sketch008]
  FullyConstrained = true
  MakeInternals = false
  MapMode = 5
  expr: Constraints[37] = <<sheet>>.LidWallAroundSides
  expr: Constraints[38] = .Constraints.Margin
  sketch-geometry (18):
    g0: LineSegment StartX=-50 StartY=51 StartZ=0 EndX=-50 EndY=-51 EndZ=0
    g1: LineSegment StartX=-47.5 StartY=-53.5 StartZ=0 EndX=47.5 EndY=-53.5 EndZ=0
    g2: LineSegment StartX=50 StartY=-51 StartZ=0 EndX=50 EndY=51 EndZ=0
    g3: LineSegment StartX=47.5 StartY=53.5 StartZ=0 EndX=-47.5 EndY=53.5 EndZ=0
    g4: ArcOfCircle CenterX=-47.5 CenterY=51 CenterZ=0 NormalX=0 NormalY=0 NormalZ=1 AngleXU=0 Radius=2.5 StartAngle=1.5708 EndAngle=3.14159
    g5: ArcOfCircle CenterX=-47.5 CenterY=-51 CenterZ=0 NormalX=0 NormalY=0 NormalZ=1 AngleXU=0 Radius=2.5 StartAngle=3.14159 EndAngle=4.71239
    g6: ArcOfCircle CenterX=47.5 CenterY=-51 CenterZ=0 NormalX=0 NormalY=0 NormalZ=1 AngleXU=0 Radius=2.5 StartAngle=4.71239 EndAngle=6.28319
    g7: ArcOfCircle CenterX=47.5 CenterY=51 CenterZ=0 NormalX=0 NormalY=0 NormalZ=1 AngleXU=0 Radius=2.5 StartAngle=-9e-16 EndAngle=1.5708
    g8: LineSegment StartX=-48.9 StartY=51 StartZ=0 EndX=-48.9 EndY=-51 EndZ=0
    g9: LineSegment StartX=-47.5 StartY=-52.4 StartZ=0 EndX=47.5 EndY=-52.4 EndZ=0
    g10: LineSegment StartX=48.9 StartY=-51 StartZ=0 EndX=48.9 EndY=51 EndZ=0
    g11: LineSegment StartX=47.5 StartY=52.4 StartZ=0 EndX=-47.5 EndY=52.4 EndZ=0
    g12: ArcOfCircle CenterX=-47.5 CenterY=51 CenterZ=0 NormalX=0 NormalY=0 NormalZ=1 AngleXU=0 Radius=1.4 StartAngle=1.5708 EndAngle=3.14159
    g13: ArcOfCircle CenterX=-47.5 CenterY=-51 CenterZ=0 NormalX=0 NormalY=0 NormalZ=1 AngleXU=0 Radius=1.4 StartAngle=3.14159 EndAngle=4.71239
    g14: ArcOfCircle CenterX=47.5 CenterY=-51 CenterZ=0 NormalX=0 NormalY=0 NormalZ=1 AngleXU=0 Radius=1.4 StartAngle=4.71239 EndAngle=6.28319
    g15: ArcOfCircle CenterX=47.5 CenterY=51 CenterZ=0 NormalX=0 NormalY=0 NormalZ=1 AngleXU=0 Radius=1.4 StartAngle=-9e-16 EndAngle=1.5708
    g16: GeomPoint [constr] X=-50 Y=53.5 Z=0
    g17: GeomPoint [constr] X=50 Y=-53.5 Z=0
  constraints (40):
    c: Tangent(g0,g4) = -1.5708
    c: Tangent(g0,g5) = -1.5708
    c: Tangent(g1,g5) = -1.5708
    c: Tangent(g1,g6) = -1.5708
    c: Tangent(g2,g6) = -1.5708
    c: Tangent(g2,g7) = -1.5708
    c: Tangent(g3,g7) = -1.5708
    c: Tangent(g3,g4) = -1.5708
    c: Vertical(g0)
    c: Vertical(g2)
    c: Horizontal(g1)
    c: Horizontal(g3)
    c: Equal(g4,g5)
    c: Equal(g5,g6)
    c: Equal(g6,g7)
    c: Tangent(g8,g12) = -1.5708
    c: Tangent(g8,g13) = -1.5708
    c: Tangent(g9,g13) = -1.5708
    c: Tangent(g9,g14) = -1.5708
    c: Tangent(g10,g14) = -1.5708
    c: Tangent(g10,g15) = -1.5708
    c: Tangent(g11,g15) = -1.5708
    c: Tangent(g11,g12) = -1.5708
    c: Coincident(g4,g12)
    c: Coincident(g5,g13)
    c: Coincident(g6,g14)
    c: Coincident(g7,g15)
    c: Vertical(g8)
    c: Vertical(g10)
    c: Horizontal(g9)
    c: PointOnObject(g16,g0)
    c: PointOnObject(g16,g3)
    c: PointOnObject(g17,g1)
    c: PointOnObject(g17,g2)
    c: DistanceX(g10,g-4) = 0.1  'Margin'
    c: Horizontal(g10,g-4)
    c: Vertical(g3,g-3)
    c: DistanceY(g-3,g3) = 1
    c: Distance(g8,g-5) = 0.1
    c: Horizontal(g8,g-5)
FEATURE [PartDesign::Pad] Pad013  label="SealOuterwall"
  BaseFeature = -> Pad007
  Direction = (0,0,1)
  Length = 4
  Length2 = 10
  Profile = -> Sketch019
  ReferenceAxis = -> Sketch019 [N_Axis]
  Suppressed = false
  Type = 0
FEATURE [PartDesign::Body] Body001  label="Seal"
  AllowCompound = false
  Group = -> [Sketch008,Pad006,Sketch009,DatumPlane001,Sketch010,AdditiveLoft,Sketch011,Binder,Pocket002,Sketch012,Pad007,Sketch019,Pad013]
  Origin = -> Origin001
  Placement = pos=(-3.2e-15,0,36.6) rot=(0,1,0;3.14159rad)
  Tip = -> Pad013
FEATURE [PartDesign::Pad] Pad014  label="BoxBatteryClip2"
  BaseFeature = -> Pocket001
  Direction = (1,0,0)
  Length = 1
  Length2 = 10
  Profile = -> Sketch006
  ReferenceAxis = -> Sketch006 [N_Axis]
  Suppressed = false
  Type = 0
FEATURE [PartDesign::Body] Body  label="Box"
  AllowCompound = false
  Group = -> [Sketch,Pad,Sketch001,Pad001,Sketch002,Pad002,Sketch003,Pad003,Sketch004,Pocket,Sketch005,Pad004,Sketch006,DatumPlane,Sketch007,Pocket001,Pad014]
  Origin = -> Origin
  Tip = -> Pad014
